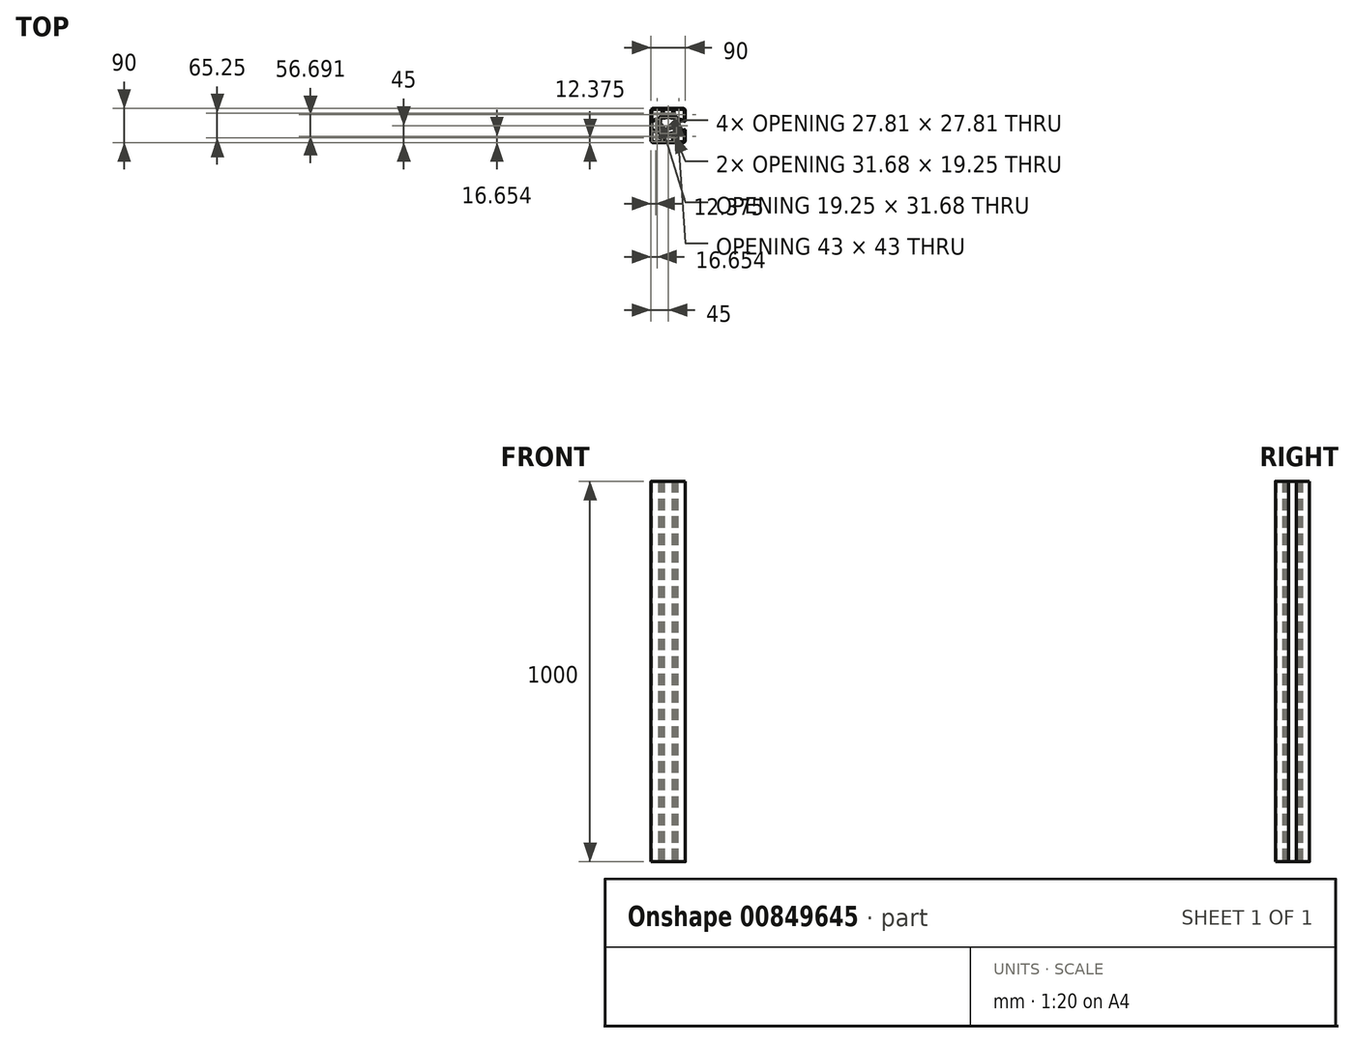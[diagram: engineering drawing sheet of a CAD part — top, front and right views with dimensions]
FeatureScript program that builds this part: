
annotation { "Feature Type Name" : "Feature", "Feature Type Description" : "" }
export const myFeature = defineFeature(function(context is Context, id is Id, definition is map)
    precondition{}
    {
        {
            var Q0;
            Q0=qCreatedBy(makeId("Top.planeOp"),FACE);
            var sketch = newSketch(context, id + "F0", { "sketchPlane" : qUnion([Q0])});
            skLineSegment(sketch, "E0", {"start": v(-42.25, -10.99) * mm, "end": v(-42.25, 10.99) * mm});
            skLineSegment(sketch, "E1", {"start": v(-24.26, -15.8) * mm, "end": v(-42.25, -10.99) * mm});
            skLineSegment(sketch, "E2", {"start": v(-23, -9.27) * mm, "end": v(-23, -14.84) * mm});
            skLineSegment(sketch, "E3", {"start": v(-23, 14.84) * mm, "end": v(-23, 9.27) * mm});
            skLineSegment(sketch, "E4", {"start": v(-42.25, 10.99) * mm, "end": v(-24.26, 15.8) * mm});
            skLineSegment(sketch, "E5", {"start": v(-39.73, -14.5) * mm, "end": v(-24.48, -18.6) * mm});
            skLineSegment(sketch, "E6", {"start": v(-42.25, -39) * mm, "end": v(-42.25, -16.44) * mm});
            skLineSegment(sketch, "E7", {"start": v(-16.44, -42.25) * mm, "end": v(-39, -42.25) * mm});
            skLineSegment(sketch, "E8", {"start": v(-18.6, -24.48) * mm, "end": v(-14.5, -39.73) * mm});
            skLineSegment(sketch, "E9", {"start": v(-21, -23) * mm, "end": v(-20.53, -23) * mm});
            skLineSegment(sketch, "E10", {"start": v(-23, -20.53) * mm, "end": v(-23, -21) * mm});
            skLineSegment(sketch, "E11", {"start": v(14.5, -39.73) * mm, "end": v(18.6, -24.48) * mm});
            skLineSegment(sketch, "E12", {"start": v(39, -42.25) * mm, "end": v(16.44, -42.25) * mm});
            skLineSegment(sketch, "E13", {"start": v(42.25, -16.44) * mm, "end": v(42.25, -39) * mm});
            skLineSegment(sketch, "E14", {"start": v(24.48, -18.6) * mm, "end": v(39.73, -14.5) * mm});
            skLineSegment(sketch, "E15", {"start": v(23, -21) * mm, "end": v(23, -20.53) * mm});
            skLineSegment(sketch, "E16", {"start": v(20.53, -23) * mm, "end": v(21, -23) * mm});
            skLineSegment(sketch, "E17", {"start": v(14.84, 23) * mm, "end": v(9.27, 23) * mm});
            skLineSegment(sketch, "E18", {"start": v(10.99, 42.25) * mm, "end": v(15.8, 24.26) * mm});
            skLineSegment(sketch, "E19", {"start": v(-10.99, 42.25) * mm, "end": v(10.99, 42.25) * mm});
            skLineSegment(sketch, "E20", {"start": v(-15.8, 24.26) * mm, "end": v(-10.99, 42.25) * mm});
            skLineSegment(sketch, "E21", {"start": v(-9.27, 23) * mm, "end": v(-14.84, 23) * mm});
            skLineSegment(sketch, "E22", {"start": v(23, 14.84) * mm, "end": v(23, 9.27) * mm});
            skLineSegment(sketch, "E23", {"start": v(23, -9.27) * mm, "end": v(23, -14.84) * mm});
            skLineSegment(sketch, "E24", {"start": v(24.26, -15.8) * mm, "end": v(43.43, -10.67) * mm});
            skLineSegment(sketch, "E25", {"start": v(45, -11.88) * mm, "end": v(45, -39) * mm});
            skLineSegment(sketch, "E26", {"start": v(39, -45) * mm, "end": v(-39, -45) * mm});
            skLineSegment(sketch, "E27", {"start": v(-45, -39) * mm, "end": v(-45, 39) * mm});
            skLineSegment(sketch, "E28", {"start": v(-39, 45) * mm, "end": v(39, 45) * mm});
            skLineSegment(sketch, "E29", {"start": v(45, 39) * mm, "end": v(45, 11.88) * mm});
            skLineSegment(sketch, "E30", {"start": v(43.43, 10.67) * mm, "end": v(24.26, 15.8) * mm});
            skLineSegment(sketch, "E31", {"start": v(20.25, 19.25) * mm, "end": v(20.25, 7.4) * mm});
            skLineSegment(sketch, "E32", {"start": v(7.4, 20.25) * mm, "end": v(19.25, 20.25) * mm});
            skLineSegment(sketch, "E33", {"start": v(-19.25, 20.25) * mm, "end": v(-7.4, 20.25) * mm});
            skLineSegment(sketch, "E34", {"start": v(-20.25, 7.4) * mm, "end": v(-20.25, 19.25) * mm});
            skLineSegment(sketch, "E35", {"start": v(-20.25, -19.25) * mm, "end": v(-20.25, -7.4) * mm});
            skLineSegment(sketch, "E36", {"start": v(-7.4, -20.25) * mm, "end": v(-19.25, -20.25) * mm});
            skLineSegment(sketch, "E37", {"start": v(19.25, -20.25) * mm, "end": v(7.4, -20.25) * mm});
            skLineSegment(sketch, "E38", {"start": v(20.25, -7.4) * mm, "end": v(20.25, -19.25) * mm});
            skLineSegment(sketch, "E39", {"start": v(39.73, 14.5) * mm, "end": v(24.48, 18.6) * mm});
            skLineSegment(sketch, "E40", {"start": v(42.25, 39) * mm, "end": v(42.25, 16.44) * mm});
            skLineSegment(sketch, "E41", {"start": v(16.44, 42.25) * mm, "end": v(39, 42.25) * mm});
            skLineSegment(sketch, "E42", {"start": v(18.6, 24.48) * mm, "end": v(14.5, 39.73) * mm});
            skLineSegment(sketch, "E43", {"start": v(21, 23) * mm, "end": v(20.53, 23) * mm});
            skLineSegment(sketch, "E44", {"start": v(23, 20.53) * mm, "end": v(23, 21) * mm});
            skLineSegment(sketch, "E45", {"start": v(-14.5, 39.73) * mm, "end": v(-18.6, 24.48) * mm});
            skLineSegment(sketch, "E46", {"start": v(-39, 42.25) * mm, "end": v(-16.44, 42.25) * mm});
            skLineSegment(sketch, "E47", {"start": v(-42.25, 16.44) * mm, "end": v(-42.25, 39) * mm});
            skLineSegment(sketch, "E48", {"start": v(-24.48, 18.6) * mm, "end": v(-39.73, 14.5) * mm});
            skLineSegment(sketch, "E49", {"start": v(-23, 21) * mm, "end": v(-23, 20.53) * mm});
            skLineSegment(sketch, "E50", {"start": v(-20.53, 23) * mm, "end": v(-21, 23) * mm});
            skLineSegment(sketch, "E51", {"start": v(10.99, -42.25) * mm, "end": v(-10.99, -42.25) * mm});
            skLineSegment(sketch, "E52", {"start": v(15.8, -24.26) * mm, "end": v(10.99, -42.25) * mm});
            skLineSegment(sketch, "E53", {"start": v(9.27, -23) * mm, "end": v(14.84, -23) * mm});
            skLineSegment(sketch, "E54", {"start": v(-14.84, -23) * mm, "end": v(-9.27, -23) * mm});
            skLineSegment(sketch, "E55", {"start": v(-10.99, -42.25) * mm, "end": v(-15.8, -24.26) * mm});
            skArc(sketch, "E56", {"start": v(-24.26, -15.8) * mm, "mid": v(-23.4, -15.64) * mm, "end": v(-23, -14.84) * mm});
            skArc(sketch, "E57", {"start": v(-23, -9.27) * mm, "mid": v(-23.02, -9.06) * mm, "end": v(-23.09, -8.86) * mm});
            skArc(sketch, "E58", {"start": v(-23.09, 8.86) * mm, "mid": v(-25, 0) * mm, "end": v(-23.09, -8.86) * mm});
            skArc(sketch, "E59", {"start": v(-23.09, 8.86) * mm, "mid": v(-23.02, 9.06) * mm, "end": v(-23, 9.27) * mm});
            skArc(sketch, "E60", {"start": v(-23, 14.84) * mm, "mid": v(-23.4, 15.64) * mm, "end": v(-24.26, 15.8) * mm});
            skArc(sketch, "E61", {"start": v(-23, -20.53) * mm, "mid": v(-23.41, -19.3) * mm, "end": v(-24.48, -18.6) * mm});
            skArc(sketch, "E62", {"start": v(-39.73, -14.5) * mm, "mid": v(-41.47, -14.85) * mm, "end": v(-42.25, -16.44) * mm});
            skArc(sketch, "E63", {"start": v(-42.25, -39) * mm, "mid": v(-41.3, -41.3) * mm, "end": v(-39, -42.25) * mm});
            skArc(sketch, "E64", {"start": v(-16.44, -42.25) * mm, "mid": v(-14.85, -41.47) * mm, "end": v(-14.5, -39.73) * mm});
            skArc(sketch, "E65", {"start": v(-18.6, -24.48) * mm, "mid": v(-19.3, -23.41) * mm, "end": v(-20.53, -23) * mm});
            skArc(sketch, "E66", {"start": v(-23, -21) * mm, "mid": v(-22.41, -22.41) * mm, "end": v(-21, -23) * mm});
            skArc(sketch, "E67", {"start": v(20.53, -23) * mm, "mid": v(19.3, -23.41) * mm, "end": v(18.6, -24.48) * mm});
            skArc(sketch, "E68", {"start": v(14.5, -39.73) * mm, "mid": v(14.85, -41.47) * mm, "end": v(16.44, -42.25) * mm});
            skArc(sketch, "E69", {"start": v(39, -42.25) * mm, "mid": v(41.3, -41.3) * mm, "end": v(42.25, -39) * mm});
            skArc(sketch, "E70", {"start": v(42.25, -16.44) * mm, "mid": v(41.47, -14.85) * mm, "end": v(39.73, -14.5) * mm});
            skArc(sketch, "E71", {"start": v(24.48, -18.6) * mm, "mid": v(23.41, -19.3) * mm, "end": v(23, -20.53) * mm});
            skArc(sketch, "E72", {"start": v(21, -23) * mm, "mid": v(22.41, -22.41) * mm, "end": v(23, -21) * mm});
            skArc(sketch, "E73", {"start": v(-9.27, 23) * mm, "mid": v(-9.06, 23.02) * mm, "end": v(-8.86, 23.09) * mm});
            skArc(sketch, "E74", {"start": v(8.86, 23.09) * mm, "mid": v(0, 25) * mm, "end": v(-8.86, 23.09) * mm});
            skArc(sketch, "E75", {"start": v(8.86, 23.09) * mm, "mid": v(9.06, 23.02) * mm, "end": v(9.27, 23) * mm});
            skArc(sketch, "E76", {"start": v(14.84, 23) * mm, "mid": v(15.64, 23.4) * mm, "end": v(15.8, 24.26) * mm});
            skArc(sketch, "E77", {"start": v(-15.8, 24.26) * mm, "mid": v(-15.64, 23.4) * mm, "end": v(-14.84, 23) * mm});
            skArc(sketch, "E78", {"start": v(24.26, 15.8) * mm, "mid": v(23.4, 15.64) * mm, "end": v(23, 14.84) * mm});
            skArc(sketch, "E79", {"start": v(23, 9.27) * mm, "mid": v(23.02, 9.06) * mm, "end": v(23.09, 8.86) * mm});
            skArc(sketch, "E80", {"start": v(23.09, -8.86) * mm, "mid": v(25, 0) * mm, "end": v(23.09, 8.86) * mm});
            skArc(sketch, "E81", {"start": v(23.09, -8.86) * mm, "mid": v(23.02, -9.06) * mm, "end": v(23, -9.27) * mm});
            skArc(sketch, "E82", {"start": v(23, -14.84) * mm, "mid": v(23.4, -15.64) * mm, "end": v(24.26, -15.8) * mm});
            skArc(sketch, "E83", {"start": v(45, -11.88) * mm, "mid": v(44.51, -10.89) * mm, "end": v(43.43, -10.67) * mm});
            skArc(sketch, "E84", {"start": v(39, -45) * mm, "mid": v(43.24, -43.24) * mm, "end": v(45, -39) * mm});
            skArc(sketch, "E85", {"start": v(-45, -39) * mm, "mid": v(-43.24, -43.24) * mm, "end": v(-39, -45) * mm});
            skArc(sketch, "E86", {"start": v(-39, 45) * mm, "mid": v(-43.24, 43.24) * mm, "end": v(-45, 39) * mm});
            skArc(sketch, "E87", {"start": v(45, 39) * mm, "mid": v(43.24, 43.24) * mm, "end": v(39, 45) * mm});
            skArc(sketch, "E88", {"start": v(43.43, 10.67) * mm, "mid": v(44.51, 10.89) * mm, "end": v(45, 11.88) * mm});
            skArc(sketch, "E89", {"start": v(20.25, 7.4) * mm, "mid": v(20.26, 7.23) * mm, "end": v(20.3, 7.07) * mm});
            skArc(sketch, "E90", {"start": v(20.25, 19.25) * mm, "mid": v(19.96, 19.96) * mm, "end": v(19.25, 20.25) * mm});
            skArc(sketch, "E91", {"start": v(7.07, 20.3) * mm, "mid": v(7.23, 20.26) * mm, "end": v(7.4, 20.25) * mm});
            skArc(sketch, "E92", {"start": v(7.07, 20.3) * mm, "mid": v(0, 21.5) * mm, "end": v(-7.07, 20.3) * mm});
            skArc(sketch, "E93", {"start": v(-7.4, 20.25) * mm, "mid": v(-7.23, 20.26) * mm, "end": v(-7.07, 20.3) * mm});
            skArc(sketch, "E94", {"start": v(-19.25, 20.25) * mm, "mid": v(-19.96, 19.96) * mm, "end": v(-20.25, 19.25) * mm});
            skArc(sketch, "E95", {"start": v(-20.3, 7.07) * mm, "mid": v(-20.26, 7.23) * mm, "end": v(-20.25, 7.4) * mm});
            skArc(sketch, "E96", {"start": v(-20.3, 7.07) * mm, "mid": v(-21.5, 0) * mm, "end": v(-20.3, -7.07) * mm});
            skArc(sketch, "E97", {"start": v(-20.25, -7.4) * mm, "mid": v(-20.26, -7.23) * mm, "end": v(-20.3, -7.07) * mm});
            skArc(sketch, "E98", {"start": v(-20.25, -19.25) * mm, "mid": v(-19.96, -19.96) * mm, "end": v(-19.25, -20.25) * mm});
            skArc(sketch, "E99", {"start": v(-7.07, -20.3) * mm, "mid": v(-7.23, -20.26) * mm, "end": v(-7.4, -20.25) * mm});
            skArc(sketch, "E100", {"start": v(-7.07, -20.3) * mm, "mid": v(0, -21.5) * mm, "end": v(7.07, -20.3) * mm});
            skArc(sketch, "E101", {"start": v(7.4, -20.25) * mm, "mid": v(7.23, -20.26) * mm, "end": v(7.07, -20.3) * mm});
            skArc(sketch, "E102", {"start": v(19.25, -20.25) * mm, "mid": v(19.96, -19.96) * mm, "end": v(20.25, -19.25) * mm});
            skArc(sketch, "E103", {"start": v(20.3, -7.07) * mm, "mid": v(20.26, -7.23) * mm, "end": v(20.25, -7.4) * mm});
            skArc(sketch, "E104", {"start": v(20.3, -7.07) * mm, "mid": v(21.5, 0) * mm, "end": v(20.3, 7.07) * mm});
            skArc(sketch, "E105", {"start": v(23, 20.53) * mm, "mid": v(23.41, 19.3) * mm, "end": v(24.48, 18.6) * mm});
            skArc(sketch, "E106", {"start": v(39.73, 14.5) * mm, "mid": v(41.47, 14.85) * mm, "end": v(42.25, 16.44) * mm});
            skArc(sketch, "E107", {"start": v(42.25, 39) * mm, "mid": v(41.3, 41.3) * mm, "end": v(39, 42.25) * mm});
            skArc(sketch, "E108", {"start": v(16.44, 42.25) * mm, "mid": v(14.85, 41.47) * mm, "end": v(14.5, 39.73) * mm});
            skArc(sketch, "E109", {"start": v(18.6, 24.48) * mm, "mid": v(19.3, 23.41) * mm, "end": v(20.53, 23) * mm});
            skArc(sketch, "E110", {"start": v(23, 21) * mm, "mid": v(22.41, 22.41) * mm, "end": v(21, 23) * mm});
            skArc(sketch, "E111", {"start": v(-20.53, 23) * mm, "mid": v(-19.3, 23.41) * mm, "end": v(-18.6, 24.48) * mm});
            skArc(sketch, "E112", {"start": v(-14.5, 39.73) * mm, "mid": v(-14.85, 41.47) * mm, "end": v(-16.44, 42.25) * mm});
            skArc(sketch, "E113", {"start": v(-39, 42.25) * mm, "mid": v(-41.3, 41.3) * mm, "end": v(-42.25, 39) * mm});
            skArc(sketch, "E114", {"start": v(-42.25, 16.44) * mm, "mid": v(-41.47, 14.85) * mm, "end": v(-39.73, 14.5) * mm});
            skArc(sketch, "E115", {"start": v(-24.48, 18.6) * mm, "mid": v(-23.41, 19.3) * mm, "end": v(-23, 20.53) * mm});
            skArc(sketch, "E116", {"start": v(-21, 23) * mm, "mid": v(-22.41, 22.41) * mm, "end": v(-23, 21) * mm});
            skArc(sketch, "E117", {"start": v(15.8, -24.26) * mm, "mid": v(15.64, -23.4) * mm, "end": v(14.84, -23) * mm});
            skArc(sketch, "E118", {"start": v(9.27, -23) * mm, "mid": v(9.06, -23.02) * mm, "end": v(8.86, -23.09) * mm});
            skArc(sketch, "E119", {"start": v(-8.86, -23.09) * mm, "mid": v(-9.06, -23.02) * mm, "end": v(-9.27, -23) * mm});
            skArc(sketch, "E120", {"start": v(-14.84, -23) * mm, "mid": v(-15.64, -23.4) * mm, "end": v(-15.8, -24.26) * mm});
            skArc(sketch, "E121", {"start": v(-8.86, -23.09) * mm, "mid": v(0, -25) * mm, "end": v(8.86, -23.09) * mm});
            skArc(sketch, "E122.1.0.0", {"start": v(55, -39) * mm, "mid": v(56.76, -43.24) * mm, "end": v(61, -45) * mm});
            skLineSegment(sketch, "E122.1.0.1", {"start": v(55, -39) * mm, "end": v(55, 39) * mm});
            skArc(sketch, "E122.1.0.2", {"start": v(57.75, -39) * mm, "mid": v(58.7, -41.3) * mm, "end": v(61, -42.25) * mm});
            skLineSegment(sketch, "E122.1.0.3", {"start": v(139, -45) * mm, "end": v(61, -45) * mm});
            skLineSegment(sketch, "E122.1.0.4", {"start": v(57.75, -39) * mm, "end": v(57.75, -16.44) * mm});
            skLineSegment(sketch, "E122.1.0.5", {"start": v(83.56, -42.25) * mm, "end": v(61, -42.25) * mm});
            skLineSegment(sketch, "E122.1.0.6", {"start": v(61, 45) * mm, "end": v(139, 45) * mm});
            skArc(sketch, "E122.1.0.7", {"start": v(145, 39) * mm, "mid": v(143.24, 43.24) * mm, "end": v(139, 45) * mm});
            skLineSegment(sketch, "E122.1.0.8", {"start": v(145, 39) * mm, "end": v(145, 11.88) * mm});
            skLineSegment(sketch, "E122.1.0.9", {"start": v(142.25, 39) * mm, "end": v(142.25, 16.44) * mm});
            skLineSegment(sketch, "E122.1.0.10", {"start": v(116.44, 42.25) * mm, "end": v(139, 42.25) * mm});
            skArc(sketch, "E122.1.0.11", {"start": v(142.25, 39) * mm, "mid": v(141.3, 41.3) * mm, "end": v(139, 42.25) * mm});
            skLineSegment(sketch, "E122.1.0.12", {"start": v(57.75, -10.99) * mm, "end": v(57.75, 10.99) * mm});
            skLineSegment(sketch, "E122.1.0.13", {"start": v(89.01, 42.25) * mm, "end": v(110.99, 42.25) * mm});
            skLineSegment(sketch, "E122.1.0.14", {"start": v(142.25, -16.44) * mm, "end": v(142.25, -39) * mm});
            skLineSegment(sketch, "E122.1.0.15", {"start": v(139, -42.25) * mm, "end": v(116.44, -42.25) * mm});
            skLineSegment(sketch, "E122.1.0.16", {"start": v(145, -11.88) * mm, "end": v(145, -39) * mm});
            skArc(sketch, "E122.1.0.17", {"start": v(139, -42.25) * mm, "mid": v(141.3, -41.3) * mm, "end": v(142.25, -39) * mm});
            skArc(sketch, "E122.1.0.18", {"start": v(139, -45) * mm, "mid": v(143.24, -43.24) * mm, "end": v(145, -39) * mm});
            skArc(sketch, "E122.1.0.19", {"start": v(79.47, 23) * mm, "mid": v(80.7, 23.41) * mm, "end": v(81.4, 24.48) * mm});
            skLineSegment(sketch, "E122.1.0.20", {"start": v(60.27, -14.5) * mm, "end": v(75.52, -18.6) * mm});
            skArc(sketch, "E122.1.0.21", {"start": v(61, 42.25) * mm, "mid": v(58.7, 41.3) * mm, "end": v(57.75, 39) * mm});
            skLineSegment(sketch, "E122.1.0.22", {"start": v(57.75, 10.99) * mm, "end": v(75.74, 15.8) * mm});
            skLineSegment(sketch, "E122.1.0.23", {"start": v(57.75, 16.44) * mm, "end": v(57.75, 39) * mm});
            skArc(sketch, "E122.1.0.24", {"start": v(60.27, -14.5) * mm, "mid": v(58.53, -14.85) * mm, "end": v(57.75, -16.44) * mm});
            skLineSegment(sketch, "E122.1.0.25", {"start": v(61, 42.25) * mm, "end": v(83.56, 42.25) * mm});
            skArc(sketch, "E122.1.0.26", {"start": v(80.75, 20.25) * mm, "mid": v(80.04, 19.96) * mm, "end": v(79.75, 19.25) * mm});
            skArc(sketch, "E122.1.0.27", {"start": v(61, 45) * mm, "mid": v(56.76, 43.24) * mm, "end": v(55, 39) * mm});
            skLineSegment(sketch, "E122.1.0.28", {"start": v(75.52, 18.6) * mm, "end": v(60.27, 14.5) * mm});
            skLineSegment(sketch, "E122.1.0.29", {"start": v(75.74, -15.8) * mm, "end": v(57.75, -10.99) * mm});
            skArc(sketch, "E122.1.0.30", {"start": v(57.75, 16.44) * mm, "mid": v(58.53, 14.85) * mm, "end": v(60.27, 14.5) * mm});
            skLineSegment(sketch, "E122.1.0.31", {"start": v(85.5, 39.73) * mm, "end": v(81.4, 24.48) * mm});
            skArc(sketch, "E122.1.0.32", {"start": v(81.4, -24.48) * mm, "mid": v(80.7, -23.41) * mm, "end": v(79.47, -23) * mm});
            skLineSegment(sketch, "E122.1.0.33", {"start": v(77, -9.27) * mm, "end": v(77, -14.84) * mm});
            skArc(sketch, "E122.1.0.34", {"start": v(79.7, 7.07) * mm, "mid": v(79.74, 7.23) * mm, "end": v(79.75, 7.4) * mm});
            skLineSegment(sketch, "E122.1.0.35", {"start": v(77, 21) * mm, "end": v(77, 20.53) * mm});
            skArc(sketch, "E122.1.0.36", {"start": v(109.27, -23) * mm, "mid": v(109.06, -23.02) * mm, "end": v(108.86, -23.09) * mm});
            skArc(sketch, "E122.1.0.37", {"start": v(92.93, -20.3) * mm, "mid": v(100, -21.5) * mm, "end": v(107.07, -20.3) * mm});
            skLineSegment(sketch, "E122.1.0.38", {"start": v(80.75, 20.25) * mm, "end": v(92.6, 20.25) * mm});
            skLineSegment(sketch, "E122.1.0.39", {"start": v(114.5, -39.73) * mm, "end": v(118.6, -24.48) * mm});
            skLineSegment(sketch, "E122.1.0.40", {"start": v(110.99, -42.25) * mm, "end": v(89.01, -42.25) * mm});
            skArc(sketch, "E122.1.0.41", {"start": v(79.75, -7.4) * mm, "mid": v(79.74, -7.23) * mm, "end": v(79.7, -7.07) * mm});
            skLineSegment(sketch, "E122.1.0.42", {"start": v(81.4, -24.48) * mm, "end": v(85.5, -39.73) * mm});
            skLineSegment(sketch, "E122.1.0.43", {"start": v(79.75, -19.25) * mm, "end": v(79.75, -7.4) * mm});
            skArc(sketch, "E122.1.0.44", {"start": v(92.93, -20.3) * mm, "mid": v(92.77, -20.26) * mm, "end": v(92.6, -20.25) * mm});
            skArc(sketch, "E122.1.0.45", {"start": v(76.91, 8.86) * mm, "mid": v(75, 0) * mm, "end": v(76.91, -8.86) * mm});
            skLineSegment(sketch, "E122.1.0.46", {"start": v(85.16, -23) * mm, "end": v(90.73, -23) * mm});
            skArc(sketch, "E122.1.0.47", {"start": v(120.53, -23) * mm, "mid": v(119.3, -23.41) * mm, "end": v(118.6, -24.48) * mm});
            skArc(sketch, "E122.1.0.48", {"start": v(85.16, -23) * mm, "mid": v(84.36, -23.4) * mm, "end": v(84.2, -24.26) * mm});
            skLineSegment(sketch, "E122.1.0.49", {"start": v(115.8, -24.26) * mm, "end": v(110.99, -42.25) * mm});
            skArc(sketch, "E122.1.0.50", {"start": v(75.52, 18.6) * mm, "mid": v(76.59, 19.3) * mm, "end": v(77, 20.53) * mm});
            skArc(sketch, "E122.1.0.51", {"start": v(83.56, -42.25) * mm, "mid": v(85.15, -41.47) * mm, "end": v(85.5, -39.73) * mm});
            skArc(sketch, "E122.1.0.52", {"start": v(77, -9.27) * mm, "mid": v(76.98, -9.06) * mm, "end": v(76.91, -8.86) * mm});
            skArc(sketch, "E122.1.0.53", {"start": v(107.4, -20.25) * mm, "mid": v(107.23, -20.26) * mm, "end": v(107.07, -20.3) * mm});
            skArc(sketch, "E122.1.0.54", {"start": v(79.7, 7.07) * mm, "mid": v(78.5, 0) * mm, "end": v(79.7, -7.07) * mm});
            skLineSegment(sketch, "E122.1.0.55", {"start": v(90.73, 23) * mm, "end": v(85.16, 23) * mm});
            skArc(sketch, "E122.1.0.56", {"start": v(91.14, -23.09) * mm, "mid": v(100, -25) * mm, "end": v(108.86, -23.09) * mm});
            skLineSegment(sketch, "E122.1.0.57", {"start": v(92.6, -20.25) * mm, "end": v(80.75, -20.25) * mm});
            skLineSegment(sketch, "E122.1.0.58", {"start": v(79.75, 7.4) * mm, "end": v(79.75, 19.25) * mm});
            skLineSegment(sketch, "E122.1.0.59", {"start": v(119.25, -20.25) * mm, "end": v(107.4, -20.25) * mm});
            skLineSegment(sketch, "E122.1.0.60", {"start": v(89.01, -42.25) * mm, "end": v(84.2, -24.26) * mm});
            skLineSegment(sketch, "E122.1.0.61", {"start": v(77, -20.53) * mm, "end": v(77, -21) * mm});
            skArc(sketch, "E122.1.0.62", {"start": v(114.5, -39.73) * mm, "mid": v(114.85, -41.47) * mm, "end": v(116.44, -42.25) * mm});
            skArc(sketch, "E122.1.0.63", {"start": v(91.14, -23.09) * mm, "mid": v(90.94, -23.02) * mm, "end": v(90.73, -23) * mm});
            skArc(sketch, "E122.1.0.64", {"start": v(108.86, 23.09) * mm, "mid": v(100, 25) * mm, "end": v(91.14, 23.09) * mm});
            skLineSegment(sketch, "E122.1.0.65", {"start": v(109.27, -23) * mm, "end": v(114.84, -23) * mm});
            skLineSegment(sketch, "E122.1.0.66", {"start": v(77, 14.84) * mm, "end": v(77, 9.27) * mm});
            skLineSegment(sketch, "E122.1.0.67", {"start": v(79.47, 23) * mm, "end": v(79, 23) * mm});
            skArc(sketch, "E122.1.0.68", {"start": v(115.8, -24.26) * mm, "mid": v(115.64, -23.4) * mm, "end": v(114.84, -23) * mm});
            skLineSegment(sketch, "E122.1.0.69", {"start": v(84.2, 24.26) * mm, "end": v(89.01, 42.25) * mm});
            skArc(sketch, "E122.1.0.70", {"start": v(75.74, -15.8) * mm, "mid": v(76.6, -15.64) * mm, "end": v(77, -14.84) * mm});
            skLineSegment(sketch, "E122.1.0.71", {"start": v(79, -23) * mm, "end": v(79.47, -23) * mm});
            skArc(sketch, "E122.1.0.72", {"start": v(77, 14.84) * mm, "mid": v(76.6, 15.64) * mm, "end": v(75.74, 15.8) * mm});
            skArc(sketch, "E122.1.0.73", {"start": v(84.2, 24.26) * mm, "mid": v(84.36, 23.4) * mm, "end": v(85.16, 23) * mm});
            skArc(sketch, "E122.1.0.74", {"start": v(107.07, 20.3) * mm, "mid": v(100, 21.5) * mm, "end": v(92.93, 20.3) * mm});
            skArc(sketch, "E122.1.0.75", {"start": v(77, -21) * mm, "mid": v(77.59, -22.41) * mm, "end": v(79, -23) * mm});
            skArc(sketch, "E122.1.0.76", {"start": v(92.6, 20.25) * mm, "mid": v(92.77, 20.26) * mm, "end": v(92.93, 20.3) * mm});
            skArc(sketch, "E122.1.0.77", {"start": v(79, 23) * mm, "mid": v(77.59, 22.41) * mm, "end": v(77, 21) * mm});
            skArc(sketch, "E122.1.0.78", {"start": v(79.75, -19.25) * mm, "mid": v(80.04, -19.96) * mm, "end": v(80.75, -20.25) * mm});
            skArc(sketch, "E122.1.0.79", {"start": v(90.73, 23) * mm, "mid": v(90.94, 23.02) * mm, "end": v(91.14, 23.09) * mm});
            skArc(sketch, "E122.1.0.80", {"start": v(76.91, 8.86) * mm, "mid": v(76.98, 9.06) * mm, "end": v(77, 9.27) * mm});
            skArc(sketch, "E122.1.0.81", {"start": v(77, -20.53) * mm, "mid": v(76.59, -19.3) * mm, "end": v(75.52, -18.6) * mm});
            skLineSegment(sketch, "E122.1.0.82", {"start": v(139.73, 14.5) * mm, "end": v(124.48, 18.6) * mm});
            skLineSegment(sketch, "E122.1.0.83", {"start": v(118.6, 24.48) * mm, "end": v(114.5, 39.73) * mm});
            skArc(sketch, "E122.1.0.84", {"start": v(124.26, 15.8) * mm, "mid": v(123.4, 15.64) * mm, "end": v(123, 14.84) * mm});
            skArc(sketch, "E122.1.0.85", {"start": v(119.25, -20.25) * mm, "mid": v(119.96, -19.96) * mm, "end": v(120.25, -19.25) * mm});
            skLineSegment(sketch, "E122.1.0.86", {"start": v(143.43, 10.67) * mm, "end": v(124.26, 15.8) * mm});
            skArc(sketch, "E122.1.0.87", {"start": v(85.5, 39.73) * mm, "mid": v(85.15, 41.47) * mm, "end": v(83.56, 42.25) * mm});
            skArc(sketch, "E122.1.0.88", {"start": v(123, 21) * mm, "mid": v(122.41, 22.41) * mm, "end": v(121, 23) * mm});
            skArc(sketch, "E122.1.0.89", {"start": v(139.73, 14.5) * mm, "mid": v(141.47, 14.85) * mm, "end": v(142.25, 16.44) * mm});
            skArc(sketch, "E122.1.0.90", {"start": v(123.09, -8.86) * mm, "mid": v(125, 0) * mm, "end": v(123.09, 8.86) * mm});
            skArc(sketch, "E122.1.0.91", {"start": v(120.3, -7.07) * mm, "mid": v(121.5, 0) * mm, "end": v(120.3, 7.07) * mm});
            skLineSegment(sketch, "E122.1.0.92", {"start": v(114.84, 23) * mm, "end": v(109.27, 23) * mm});
            skArc(sketch, "E122.1.0.93", {"start": v(123, 9.27) * mm, "mid": v(123.02, 9.06) * mm, "end": v(123.09, 8.86) * mm});
            skLineSegment(sketch, "E122.1.0.94", {"start": v(124.26, -15.8) * mm, "end": v(143.43, -10.67) * mm});
            skArc(sketch, "E122.1.0.95", {"start": v(142.25, -16.44) * mm, "mid": v(141.47, -14.85) * mm, "end": v(139.73, -14.5) * mm});
            skArc(sketch, "E122.1.0.96", {"start": v(123.09, -8.86) * mm, "mid": v(123.02, -9.06) * mm, "end": v(123, -9.27) * mm});
            skArc(sketch, "E122.1.0.97", {"start": v(123, -14.84) * mm, "mid": v(123.4, -15.64) * mm, "end": v(124.26, -15.8) * mm});
            skArc(sketch, "E122.1.0.98", {"start": v(116.44, 42.25) * mm, "mid": v(114.85, 41.47) * mm, "end": v(114.5, 39.73) * mm});
            skArc(sketch, "E122.1.0.99", {"start": v(145, -11.88) * mm, "mid": v(144.51, -10.89) * mm, "end": v(143.43, -10.67) * mm});
            skLineSegment(sketch, "E122.1.0.100", {"start": v(123, 20.53) * mm, "end": v(123, 21) * mm});
            skLineSegment(sketch, "E122.1.0.101", {"start": v(123, -9.27) * mm, "end": v(123, -14.84) * mm});
            skLineSegment(sketch, "E122.1.0.102", {"start": v(120.25, 19.25) * mm, "end": v(120.25, 7.4) * mm});
            skLineSegment(sketch, "E122.1.0.103", {"start": v(120.25, -7.4) * mm, "end": v(120.25, -19.25) * mm});
            skLineSegment(sketch, "E122.1.0.104", {"start": v(110.99, 42.25) * mm, "end": v(115.8, 24.26) * mm});
            skLineSegment(sketch, "E122.1.0.105", {"start": v(107.4, 20.25) * mm, "end": v(119.25, 20.25) * mm});
            skArc(sketch, "E122.1.0.106", {"start": v(143.43, 10.67) * mm, "mid": v(144.51, 10.89) * mm, "end": v(145, 11.88) * mm});
            skArc(sketch, "E122.1.0.107", {"start": v(114.84, 23) * mm, "mid": v(115.64, 23.4) * mm, "end": v(115.8, 24.26) * mm});
            skLineSegment(sketch, "E122.1.0.108", {"start": v(124.48, -18.6) * mm, "end": v(139.73, -14.5) * mm});
            skLineSegment(sketch, "E122.1.0.109", {"start": v(123, 14.84) * mm, "end": v(123, 9.27) * mm});
            skArc(sketch, "E122.1.0.110", {"start": v(118.6, 24.48) * mm, "mid": v(119.3, 23.41) * mm, "end": v(120.53, 23) * mm});
            skArc(sketch, "E122.1.0.111", {"start": v(120.25, 19.25) * mm, "mid": v(119.96, 19.96) * mm, "end": v(119.25, 20.25) * mm});
            skArc(sketch, "E122.1.0.112", {"start": v(108.86, 23.09) * mm, "mid": v(109.06, 23.02) * mm, "end": v(109.27, 23) * mm});
            skArc(sketch, "E122.1.0.113", {"start": v(120.3, -7.07) * mm, "mid": v(120.26, -7.23) * mm, "end": v(120.25, -7.4) * mm});
            skArc(sketch, "E122.1.0.114", {"start": v(121, -23) * mm, "mid": v(122.41, -22.41) * mm, "end": v(123, -21) * mm});
            skArc(sketch, "E122.1.0.115", {"start": v(107.07, 20.3) * mm, "mid": v(107.23, 20.26) * mm, "end": v(107.4, 20.25) * mm});
            skArc(sketch, "E122.1.0.116", {"start": v(120.25, 7.4) * mm, "mid": v(120.26, 7.23) * mm, "end": v(120.3, 7.07) * mm});
            skArc(sketch, "E122.1.0.117", {"start": v(123, 20.53) * mm, "mid": v(123.41, 19.3) * mm, "end": v(124.48, 18.6) * mm});
            skLineSegment(sketch, "E122.1.0.118", {"start": v(123, -21) * mm, "end": v(123, -20.53) * mm});
            skLineSegment(sketch, "E122.1.0.119", {"start": v(121, 23) * mm, "end": v(120.53, 23) * mm});
            skLineSegment(sketch, "E122.1.0.120", {"start": v(120.53, -23) * mm, "end": v(121, -23) * mm});
            skArc(sketch, "E122.1.0.121", {"start": v(124.48, -18.6) * mm, "mid": v(123.41, -19.3) * mm, "end": v(123, -20.53) * mm});
            skArc(sketch, "E122.2.0.0", {"start": v(155, -39) * mm, "mid": v(156.76, -43.24) * mm, "end": v(161, -45) * mm});
            skLineSegment(sketch, "E122.2.0.1", {"start": v(155, -39) * mm, "end": v(155, 39) * mm});
            skArc(sketch, "E122.2.0.2", {"start": v(157.75, -39) * mm, "mid": v(158.7, -41.3) * mm, "end": v(161, -42.25) * mm});
            skLineSegment(sketch, "E122.2.0.3", {"start": v(239, -45) * mm, "end": v(161, -45) * mm});
            skLineSegment(sketch, "E122.2.0.4", {"start": v(157.75, -39) * mm, "end": v(157.75, -16.44) * mm});
            skLineSegment(sketch, "E122.2.0.5", {"start": v(183.56, -42.25) * mm, "end": v(161, -42.25) * mm});
            skLineSegment(sketch, "E122.2.0.6", {"start": v(161, 45) * mm, "end": v(239, 45) * mm});
            skArc(sketch, "E122.2.0.7", {"start": v(245, 39) * mm, "mid": v(243.24, 43.24) * mm, "end": v(239, 45) * mm});
            skLineSegment(sketch, "E122.2.0.8", {"start": v(245, 39) * mm, "end": v(245, 11.88) * mm});
            skLineSegment(sketch, "E122.2.0.9", {"start": v(242.25, 39) * mm, "end": v(242.25, 16.44) * mm});
            skLineSegment(sketch, "E122.2.0.10", {"start": v(216.44, 42.25) * mm, "end": v(239, 42.25) * mm});
            skArc(sketch, "E122.2.0.11", {"start": v(242.25, 39) * mm, "mid": v(241.3, 41.3) * mm, "end": v(239, 42.25) * mm});
            skLineSegment(sketch, "E122.2.0.12", {"start": v(157.75, -10.99) * mm, "end": v(157.75, 10.99) * mm});
            skLineSegment(sketch, "E122.2.0.13", {"start": v(189.01, 42.25) * mm, "end": v(210.99, 42.25) * mm});
            skLineSegment(sketch, "E122.2.0.14", {"start": v(242.25, -16.44) * mm, "end": v(242.25, -39) * mm});
            skLineSegment(sketch, "E122.2.0.15", {"start": v(239, -42.25) * mm, "end": v(216.44, -42.25) * mm});
            skLineSegment(sketch, "E122.2.0.16", {"start": v(245, -11.88) * mm, "end": v(245, -39) * mm});
            skArc(sketch, "E122.2.0.17", {"start": v(239, -42.25) * mm, "mid": v(241.3, -41.3) * mm, "end": v(242.25, -39) * mm});
            skArc(sketch, "E122.2.0.18", {"start": v(239, -45) * mm, "mid": v(243.24, -43.24) * mm, "end": v(245, -39) * mm});
            skArc(sketch, "E122.2.0.19", {"start": v(179.47, 23) * mm, "mid": v(180.7, 23.41) * mm, "end": v(181.4, 24.48) * mm});
            skLineSegment(sketch, "E122.2.0.20", {"start": v(160.27, -14.5) * mm, "end": v(175.52, -18.6) * mm});
            skArc(sketch, "E122.2.0.21", {"start": v(161, 42.25) * mm, "mid": v(158.7, 41.3) * mm, "end": v(157.75, 39) * mm});
            skLineSegment(sketch, "E122.2.0.22", {"start": v(157.75, 10.99) * mm, "end": v(175.74, 15.8) * mm});
            skLineSegment(sketch, "E122.2.0.23", {"start": v(157.75, 16.44) * mm, "end": v(157.75, 39) * mm});
            skArc(sketch, "E122.2.0.24", {"start": v(160.27, -14.5) * mm, "mid": v(158.53, -14.85) * mm, "end": v(157.75, -16.44) * mm});
            skLineSegment(sketch, "E122.2.0.25", {"start": v(161, 42.25) * mm, "end": v(183.56, 42.25) * mm});
            skArc(sketch, "E122.2.0.26", {"start": v(180.75, 20.25) * mm, "mid": v(180.04, 19.96) * mm, "end": v(179.75, 19.25) * mm});
            skArc(sketch, "E122.2.0.27", {"start": v(161, 45) * mm, "mid": v(156.76, 43.24) * mm, "end": v(155, 39) * mm});
            skLineSegment(sketch, "E122.2.0.28", {"start": v(175.52, 18.6) * mm, "end": v(160.27, 14.5) * mm});
            skLineSegment(sketch, "E122.2.0.29", {"start": v(175.74, -15.8) * mm, "end": v(157.75, -10.99) * mm});
            skArc(sketch, "E122.2.0.30", {"start": v(157.75, 16.44) * mm, "mid": v(158.53, 14.85) * mm, "end": v(160.27, 14.5) * mm});
            skLineSegment(sketch, "E122.2.0.31", {"start": v(185.5, 39.73) * mm, "end": v(181.4, 24.48) * mm});
            skArc(sketch, "E122.2.0.32", {"start": v(181.4, -24.48) * mm, "mid": v(180.7, -23.41) * mm, "end": v(179.47, -23) * mm});
            skLineSegment(sketch, "E122.2.0.33", {"start": v(177, -9.27) * mm, "end": v(177, -14.84) * mm});
            skArc(sketch, "E122.2.0.34", {"start": v(179.7, 7.07) * mm, "mid": v(179.74, 7.23) * mm, "end": v(179.75, 7.4) * mm});
            skLineSegment(sketch, "E122.2.0.35", {"start": v(177, 21) * mm, "end": v(177, 20.53) * mm});
            skArc(sketch, "E122.2.0.36", {"start": v(209.27, -23) * mm, "mid": v(209.06, -23.02) * mm, "end": v(208.86, -23.09) * mm});
            skArc(sketch, "E122.2.0.37", {"start": v(192.93, -20.3) * mm, "mid": v(200, -21.5) * mm, "end": v(207.07, -20.3) * mm});
            skLineSegment(sketch, "E122.2.0.38", {"start": v(180.75, 20.25) * mm, "end": v(192.6, 20.25) * mm});
            skLineSegment(sketch, "E122.2.0.39", {"start": v(214.5, -39.73) * mm, "end": v(218.6, -24.48) * mm});
            skLineSegment(sketch, "E122.2.0.40", {"start": v(210.99, -42.25) * mm, "end": v(189.01, -42.25) * mm});
            skArc(sketch, "E122.2.0.41", {"start": v(179.75, -7.4) * mm, "mid": v(179.74, -7.23) * mm, "end": v(179.7, -7.07) * mm});
            skLineSegment(sketch, "E122.2.0.42", {"start": v(181.4, -24.48) * mm, "end": v(185.5, -39.73) * mm});
            skLineSegment(sketch, "E122.2.0.43", {"start": v(179.75, -19.25) * mm, "end": v(179.75, -7.4) * mm});
            skArc(sketch, "E122.2.0.44", {"start": v(192.93, -20.3) * mm, "mid": v(192.77, -20.26) * mm, "end": v(192.6, -20.25) * mm});
            skArc(sketch, "E122.2.0.45", {"start": v(176.91, 8.86) * mm, "mid": v(175, 0) * mm, "end": v(176.91, -8.86) * mm});
            skLineSegment(sketch, "E122.2.0.46", {"start": v(185.16, -23) * mm, "end": v(190.73, -23) * mm});
            skArc(sketch, "E122.2.0.47", {"start": v(220.53, -23) * mm, "mid": v(219.3, -23.41) * mm, "end": v(218.6, -24.48) * mm});
            skArc(sketch, "E122.2.0.48", {"start": v(185.16, -23) * mm, "mid": v(184.36, -23.4) * mm, "end": v(184.2, -24.26) * mm});
            skLineSegment(sketch, "E122.2.0.49", {"start": v(215.8, -24.26) * mm, "end": v(210.99, -42.25) * mm});
            skArc(sketch, "E122.2.0.50", {"start": v(175.52, 18.6) * mm, "mid": v(176.59, 19.3) * mm, "end": v(177, 20.53) * mm});
            skArc(sketch, "E122.2.0.51", {"start": v(183.56, -42.25) * mm, "mid": v(185.15, -41.47) * mm, "end": v(185.5, -39.73) * mm});
            skArc(sketch, "E122.2.0.52", {"start": v(177, -9.27) * mm, "mid": v(176.98, -9.06) * mm, "end": v(176.91, -8.86) * mm});
            skArc(sketch, "E122.2.0.53", {"start": v(207.4, -20.25) * mm, "mid": v(207.23, -20.26) * mm, "end": v(207.07, -20.3) * mm});
            skArc(sketch, "E122.2.0.54", {"start": v(179.7, 7.07) * mm, "mid": v(178.5, 0) * mm, "end": v(179.7, -7.07) * mm});
            skLineSegment(sketch, "E122.2.0.55", {"start": v(190.73, 23) * mm, "end": v(185.16, 23) * mm});
            skArc(sketch, "E122.2.0.56", {"start": v(191.14, -23.09) * mm, "mid": v(200, -25) * mm, "end": v(208.86, -23.09) * mm});
            skLineSegment(sketch, "E122.2.0.57", {"start": v(192.6, -20.25) * mm, "end": v(180.75, -20.25) * mm});
            skLineSegment(sketch, "E122.2.0.58", {"start": v(179.75, 7.4) * mm, "end": v(179.75, 19.25) * mm});
            skLineSegment(sketch, "E122.2.0.59", {"start": v(219.25, -20.25) * mm, "end": v(207.4, -20.25) * mm});
            skLineSegment(sketch, "E122.2.0.60", {"start": v(189.01, -42.25) * mm, "end": v(184.2, -24.26) * mm});
            skLineSegment(sketch, "E122.2.0.61", {"start": v(177, -20.53) * mm, "end": v(177, -21) * mm});
            skArc(sketch, "E122.2.0.62", {"start": v(214.5, -39.73) * mm, "mid": v(214.85, -41.47) * mm, "end": v(216.44, -42.25) * mm});
            skArc(sketch, "E122.2.0.63", {"start": v(191.14, -23.09) * mm, "mid": v(190.94, -23.02) * mm, "end": v(190.73, -23) * mm});
            skArc(sketch, "E122.2.0.64", {"start": v(208.86, 23.09) * mm, "mid": v(200, 25) * mm, "end": v(191.14, 23.09) * mm});
            skLineSegment(sketch, "E122.2.0.65", {"start": v(209.27, -23) * mm, "end": v(214.84, -23) * mm});
            skLineSegment(sketch, "E122.2.0.66", {"start": v(177, 14.84) * mm, "end": v(177, 9.27) * mm});
            skLineSegment(sketch, "E122.2.0.67", {"start": v(179.47, 23) * mm, "end": v(179, 23) * mm});
            skArc(sketch, "E122.2.0.68", {"start": v(215.8, -24.26) * mm, "mid": v(215.64, -23.4) * mm, "end": v(214.84, -23) * mm});
            skLineSegment(sketch, "E122.2.0.69", {"start": v(184.2, 24.26) * mm, "end": v(189.01, 42.25) * mm});
            skArc(sketch, "E122.2.0.70", {"start": v(175.74, -15.8) * mm, "mid": v(176.6, -15.64) * mm, "end": v(177, -14.84) * mm});
            skLineSegment(sketch, "E122.2.0.71", {"start": v(179, -23) * mm, "end": v(179.47, -23) * mm});
            skArc(sketch, "E122.2.0.72", {"start": v(177, 14.84) * mm, "mid": v(176.6, 15.64) * mm, "end": v(175.74, 15.8) * mm});
            skArc(sketch, "E122.2.0.73", {"start": v(184.2, 24.26) * mm, "mid": v(184.36, 23.4) * mm, "end": v(185.16, 23) * mm});
            skArc(sketch, "E122.2.0.74", {"start": v(207.07, 20.3) * mm, "mid": v(200, 21.5) * mm, "end": v(192.93, 20.3) * mm});
            skArc(sketch, "E122.2.0.75", {"start": v(177, -21) * mm, "mid": v(177.59, -22.41) * mm, "end": v(179, -23) * mm});
            skArc(sketch, "E122.2.0.76", {"start": v(192.6, 20.25) * mm, "mid": v(192.77, 20.26) * mm, "end": v(192.93, 20.3) * mm});
            skArc(sketch, "E122.2.0.77", {"start": v(179, 23) * mm, "mid": v(177.59, 22.41) * mm, "end": v(177, 21) * mm});
            skArc(sketch, "E122.2.0.78", {"start": v(179.75, -19.25) * mm, "mid": v(180.04, -19.96) * mm, "end": v(180.75, -20.25) * mm});
            skArc(sketch, "E122.2.0.79", {"start": v(190.73, 23) * mm, "mid": v(190.94, 23.02) * mm, "end": v(191.14, 23.09) * mm});
            skArc(sketch, "E122.2.0.80", {"start": v(176.91, 8.86) * mm, "mid": v(176.98, 9.06) * mm, "end": v(177, 9.27) * mm});
            skArc(sketch, "E122.2.0.81", {"start": v(177, -20.53) * mm, "mid": v(176.59, -19.3) * mm, "end": v(175.52, -18.6) * mm});
            skLineSegment(sketch, "E122.2.0.82", {"start": v(239.73, 14.5) * mm, "end": v(224.48, 18.6) * mm});
            skLineSegment(sketch, "E122.2.0.83", {"start": v(218.6, 24.48) * mm, "end": v(214.5, 39.73) * mm});
            skArc(sketch, "E122.2.0.84", {"start": v(224.26, 15.8) * mm, "mid": v(223.4, 15.64) * mm, "end": v(223, 14.84) * mm});
            skArc(sketch, "E122.2.0.85", {"start": v(219.25, -20.25) * mm, "mid": v(219.96, -19.96) * mm, "end": v(220.25, -19.25) * mm});
            skLineSegment(sketch, "E122.2.0.86", {"start": v(243.43, 10.67) * mm, "end": v(224.26, 15.8) * mm});
            skArc(sketch, "E122.2.0.87", {"start": v(185.5, 39.73) * mm, "mid": v(185.15, 41.47) * mm, "end": v(183.56, 42.25) * mm});
            skArc(sketch, "E122.2.0.88", {"start": v(223, 21) * mm, "mid": v(222.41, 22.41) * mm, "end": v(221, 23) * mm});
            skArc(sketch, "E122.2.0.89", {"start": v(239.73, 14.5) * mm, "mid": v(241.47, 14.85) * mm, "end": v(242.25, 16.44) * mm});
            skArc(sketch, "E122.2.0.90", {"start": v(223.09, -8.86) * mm, "mid": v(225, 0) * mm, "end": v(223.09, 8.86) * mm});
            skArc(sketch, "E122.2.0.91", {"start": v(220.3, -7.07) * mm, "mid": v(221.5, 0) * mm, "end": v(220.3, 7.07) * mm});
            skLineSegment(sketch, "E122.2.0.92", {"start": v(214.84, 23) * mm, "end": v(209.27, 23) * mm});
            skArc(sketch, "E122.2.0.93", {"start": v(223, 9.27) * mm, "mid": v(223.02, 9.06) * mm, "end": v(223.09, 8.86) * mm});
            skLineSegment(sketch, "E122.2.0.94", {"start": v(224.26, -15.8) * mm, "end": v(243.43, -10.67) * mm});
            skArc(sketch, "E122.2.0.95", {"start": v(242.25, -16.44) * mm, "mid": v(241.47, -14.85) * mm, "end": v(239.73, -14.5) * mm});
            skArc(sketch, "E122.2.0.96", {"start": v(223.09, -8.86) * mm, "mid": v(223.02, -9.06) * mm, "end": v(223, -9.27) * mm});
            skArc(sketch, "E122.2.0.97", {"start": v(223, -14.84) * mm, "mid": v(223.4, -15.64) * mm, "end": v(224.26, -15.8) * mm});
            skArc(sketch, "E122.2.0.98", {"start": v(216.44, 42.25) * mm, "mid": v(214.85, 41.47) * mm, "end": v(214.5, 39.73) * mm});
            skArc(sketch, "E122.2.0.99", {"start": v(245, -11.88) * mm, "mid": v(244.51, -10.89) * mm, "end": v(243.43, -10.67) * mm});
            skLineSegment(sketch, "E122.2.0.100", {"start": v(223, 20.53) * mm, "end": v(223, 21) * mm});
            skLineSegment(sketch, "E122.2.0.101", {"start": v(223, -9.27) * mm, "end": v(223, -14.84) * mm});
            skLineSegment(sketch, "E122.2.0.102", {"start": v(220.25, 19.25) * mm, "end": v(220.25, 7.4) * mm});
            skLineSegment(sketch, "E122.2.0.103", {"start": v(220.25, -7.4) * mm, "end": v(220.25, -19.25) * mm});
            skLineSegment(sketch, "E122.2.0.104", {"start": v(210.99, 42.25) * mm, "end": v(215.8, 24.26) * mm});
            skLineSegment(sketch, "E122.2.0.105", {"start": v(207.4, 20.25) * mm, "end": v(219.25, 20.25) * mm});
            skArc(sketch, "E122.2.0.106", {"start": v(243.43, 10.67) * mm, "mid": v(244.51, 10.89) * mm, "end": v(245, 11.88) * mm});
            skArc(sketch, "E122.2.0.107", {"start": v(214.84, 23) * mm, "mid": v(215.64, 23.4) * mm, "end": v(215.8, 24.26) * mm});
            skLineSegment(sketch, "E122.2.0.108", {"start": v(224.48, -18.6) * mm, "end": v(239.73, -14.5) * mm});
            skLineSegment(sketch, "E122.2.0.109", {"start": v(223, 14.84) * mm, "end": v(223, 9.27) * mm});
            skArc(sketch, "E122.2.0.110", {"start": v(218.6, 24.48) * mm, "mid": v(219.3, 23.41) * mm, "end": v(220.53, 23) * mm});
            skArc(sketch, "E122.2.0.111", {"start": v(220.25, 19.25) * mm, "mid": v(219.96, 19.96) * mm, "end": v(219.25, 20.25) * mm});
            skArc(sketch, "E122.2.0.112", {"start": v(208.86, 23.09) * mm, "mid": v(209.06, 23.02) * mm, "end": v(209.27, 23) * mm});
            skArc(sketch, "E122.2.0.113", {"start": v(220.3, -7.07) * mm, "mid": v(220.26, -7.23) * mm, "end": v(220.25, -7.4) * mm});
            skArc(sketch, "E122.2.0.114", {"start": v(221, -23) * mm, "mid": v(222.41, -22.41) * mm, "end": v(223, -21) * mm});
            skArc(sketch, "E122.2.0.115", {"start": v(207.07, 20.3) * mm, "mid": v(207.23, 20.26) * mm, "end": v(207.4, 20.25) * mm});
            skArc(sketch, "E122.2.0.116", {"start": v(220.25, 7.4) * mm, "mid": v(220.26, 7.23) * mm, "end": v(220.3, 7.07) * mm});
            skArc(sketch, "E122.2.0.117", {"start": v(223, 20.53) * mm, "mid": v(223.41, 19.3) * mm, "end": v(224.48, 18.6) * mm});
            skLineSegment(sketch, "E122.2.0.118", {"start": v(223, -21) * mm, "end": v(223, -20.53) * mm});
            skLineSegment(sketch, "E122.2.0.119", {"start": v(221, 23) * mm, "end": v(220.53, 23) * mm});
            skLineSegment(sketch, "E122.2.0.120", {"start": v(220.53, -23) * mm, "end": v(221, -23) * mm});
            skArc(sketch, "E122.2.0.121", {"start": v(224.48, -18.6) * mm, "mid": v(223.41, -19.3) * mm, "end": v(223, -20.53) * mm});
            skArc(sketch, "E122.3.0.0", {"start": v(255, -39) * mm, "mid": v(256.76, -43.24) * mm, "end": v(261, -45) * mm});
            skLineSegment(sketch, "E122.3.0.1", {"start": v(255, -39) * mm, "end": v(255, 39) * mm});
            skArc(sketch, "E122.3.0.2", {"start": v(257.75, -39) * mm, "mid": v(258.7, -41.3) * mm, "end": v(261, -42.25) * mm});
            skLineSegment(sketch, "E122.3.0.3", {"start": v(339, -45) * mm, "end": v(261, -45) * mm});
            skLineSegment(sketch, "E122.3.0.4", {"start": v(257.75, -39) * mm, "end": v(257.75, -16.44) * mm});
            skLineSegment(sketch, "E122.3.0.5", {"start": v(283.56, -42.25) * mm, "end": v(261, -42.25) * mm});
            skLineSegment(sketch, "E122.3.0.6", {"start": v(261, 45) * mm, "end": v(339, 45) * mm});
            skArc(sketch, "E122.3.0.7", {"start": v(345, 39) * mm, "mid": v(343.24, 43.24) * mm, "end": v(339, 45) * mm});
            skLineSegment(sketch, "E122.3.0.8", {"start": v(345, 39) * mm, "end": v(345, 11.88) * mm});
            skLineSegment(sketch, "E122.3.0.9", {"start": v(342.25, 39) * mm, "end": v(342.25, 16.44) * mm});
            skLineSegment(sketch, "E122.3.0.10", {"start": v(316.44, 42.25) * mm, "end": v(339, 42.25) * mm});
            skArc(sketch, "E122.3.0.11", {"start": v(342.25, 39) * mm, "mid": v(341.3, 41.3) * mm, "end": v(339, 42.25) * mm});
            skLineSegment(sketch, "E122.3.0.12", {"start": v(257.75, -10.99) * mm, "end": v(257.75, 10.99) * mm});
            skLineSegment(sketch, "E122.3.0.13", {"start": v(289.01, 42.25) * mm, "end": v(310.99, 42.25) * mm});
            skLineSegment(sketch, "E122.3.0.14", {"start": v(342.25, -16.44) * mm, "end": v(342.25, -39) * mm});
            skLineSegment(sketch, "E122.3.0.15", {"start": v(339, -42.25) * mm, "end": v(316.44, -42.25) * mm});
            skLineSegment(sketch, "E122.3.0.16", {"start": v(345, -11.88) * mm, "end": v(345, -39) * mm});
            skArc(sketch, "E122.3.0.17", {"start": v(339, -42.25) * mm, "mid": v(341.3, -41.3) * mm, "end": v(342.25, -39) * mm});
            skArc(sketch, "E122.3.0.18", {"start": v(339, -45) * mm, "mid": v(343.24, -43.24) * mm, "end": v(345, -39) * mm});
            skArc(sketch, "E122.3.0.19", {"start": v(279.47, 23) * mm, "mid": v(280.7, 23.41) * mm, "end": v(281.4, 24.48) * mm});
            skLineSegment(sketch, "E122.3.0.20", {"start": v(260.27, -14.5) * mm, "end": v(275.52, -18.6) * mm});
            skArc(sketch, "E122.3.0.21", {"start": v(261, 42.25) * mm, "mid": v(258.7, 41.3) * mm, "end": v(257.75, 39) * mm});
            skLineSegment(sketch, "E122.3.0.22", {"start": v(257.75, 10.99) * mm, "end": v(275.74, 15.8) * mm});
            skLineSegment(sketch, "E122.3.0.23", {"start": v(257.75, 16.44) * mm, "end": v(257.75, 39) * mm});
            skArc(sketch, "E122.3.0.24", {"start": v(260.27, -14.5) * mm, "mid": v(258.53, -14.85) * mm, "end": v(257.75, -16.44) * mm});
            skLineSegment(sketch, "E122.3.0.25", {"start": v(261, 42.25) * mm, "end": v(283.56, 42.25) * mm});
            skArc(sketch, "E122.3.0.26", {"start": v(280.75, 20.25) * mm, "mid": v(280.04, 19.96) * mm, "end": v(279.75, 19.25) * mm});
            skArc(sketch, "E122.3.0.27", {"start": v(261, 45) * mm, "mid": v(256.76, 43.24) * mm, "end": v(255, 39) * mm});
            skLineSegment(sketch, "E122.3.0.28", {"start": v(275.52, 18.6) * mm, "end": v(260.27, 14.5) * mm});
            skLineSegment(sketch, "E122.3.0.29", {"start": v(275.74, -15.8) * mm, "end": v(257.75, -10.99) * mm});
            skArc(sketch, "E122.3.0.30", {"start": v(257.75, 16.44) * mm, "mid": v(258.53, 14.85) * mm, "end": v(260.27, 14.5) * mm});
            skLineSegment(sketch, "E122.3.0.31", {"start": v(285.5, 39.73) * mm, "end": v(281.4, 24.48) * mm});
            skArc(sketch, "E122.3.0.32", {"start": v(281.4, -24.48) * mm, "mid": v(280.7, -23.41) * mm, "end": v(279.47, -23) * mm});
            skLineSegment(sketch, "E122.3.0.33", {"start": v(277, -9.27) * mm, "end": v(277, -14.84) * mm});
            skArc(sketch, "E122.3.0.34", {"start": v(279.7, 7.07) * mm, "mid": v(279.74, 7.23) * mm, "end": v(279.75, 7.4) * mm});
            skLineSegment(sketch, "E122.3.0.35", {"start": v(277, 21) * mm, "end": v(277, 20.53) * mm});
            skArc(sketch, "E122.3.0.36", {"start": v(309.27, -23) * mm, "mid": v(309.06, -23.02) * mm, "end": v(308.86, -23.09) * mm});
            skArc(sketch, "E122.3.0.37", {"start": v(292.93, -20.3) * mm, "mid": v(300, -21.5) * mm, "end": v(307.07, -20.3) * mm});
            skLineSegment(sketch, "E122.3.0.38", {"start": v(280.75, 20.25) * mm, "end": v(292.6, 20.25) * mm});
            skLineSegment(sketch, "E122.3.0.39", {"start": v(314.5, -39.73) * mm, "end": v(318.6, -24.48) * mm});
            skLineSegment(sketch, "E122.3.0.40", {"start": v(310.99, -42.25) * mm, "end": v(289.01, -42.25) * mm});
            skArc(sketch, "E122.3.0.41", {"start": v(279.75, -7.4) * mm, "mid": v(279.74, -7.23) * mm, "end": v(279.7, -7.07) * mm});
            skLineSegment(sketch, "E122.3.0.42", {"start": v(281.4, -24.48) * mm, "end": v(285.5, -39.73) * mm});
            skLineSegment(sketch, "E122.3.0.43", {"start": v(279.75, -19.25) * mm, "end": v(279.75, -7.4) * mm});
            skArc(sketch, "E122.3.0.44", {"start": v(292.93, -20.3) * mm, "mid": v(292.77, -20.26) * mm, "end": v(292.6, -20.25) * mm});
            skArc(sketch, "E122.3.0.45", {"start": v(276.91, 8.86) * mm, "mid": v(275, 0) * mm, "end": v(276.91, -8.86) * mm});
            skLineSegment(sketch, "E122.3.0.46", {"start": v(285.16, -23) * mm, "end": v(290.73, -23) * mm});
            skArc(sketch, "E122.3.0.47", {"start": v(320.53, -23) * mm, "mid": v(319.3, -23.41) * mm, "end": v(318.6, -24.48) * mm});
            skArc(sketch, "E122.3.0.48", {"start": v(285.16, -23) * mm, "mid": v(284.36, -23.4) * mm, "end": v(284.2, -24.26) * mm});
            skLineSegment(sketch, "E122.3.0.49", {"start": v(315.8, -24.26) * mm, "end": v(310.99, -42.25) * mm});
            skArc(sketch, "E122.3.0.50", {"start": v(275.52, 18.6) * mm, "mid": v(276.59, 19.3) * mm, "end": v(277, 20.53) * mm});
            skArc(sketch, "E122.3.0.51", {"start": v(283.56, -42.25) * mm, "mid": v(285.15, -41.47) * mm, "end": v(285.5, -39.73) * mm});
            skArc(sketch, "E122.3.0.52", {"start": v(277, -9.27) * mm, "mid": v(276.98, -9.06) * mm, "end": v(276.91, -8.86) * mm});
            skArc(sketch, "E122.3.0.53", {"start": v(307.4, -20.25) * mm, "mid": v(307.23, -20.26) * mm, "end": v(307.07, -20.3) * mm});
            skArc(sketch, "E122.3.0.54", {"start": v(279.7, 7.07) * mm, "mid": v(278.5, 0) * mm, "end": v(279.7, -7.07) * mm});
            skLineSegment(sketch, "E122.3.0.55", {"start": v(290.73, 23) * mm, "end": v(285.16, 23) * mm});
            skArc(sketch, "E122.3.0.56", {"start": v(291.14, -23.09) * mm, "mid": v(300, -25) * mm, "end": v(308.86, -23.09) * mm});
            skLineSegment(sketch, "E122.3.0.57", {"start": v(292.6, -20.25) * mm, "end": v(280.75, -20.25) * mm});
            skLineSegment(sketch, "E122.3.0.58", {"start": v(279.75, 7.4) * mm, "end": v(279.75, 19.25) * mm});
            skLineSegment(sketch, "E122.3.0.59", {"start": v(319.25, -20.25) * mm, "end": v(307.4, -20.25) * mm});
            skLineSegment(sketch, "E122.3.0.60", {"start": v(289.01, -42.25) * mm, "end": v(284.2, -24.26) * mm});
            skLineSegment(sketch, "E122.3.0.61", {"start": v(277, -20.53) * mm, "end": v(277, -21) * mm});
            skArc(sketch, "E122.3.0.62", {"start": v(314.5, -39.73) * mm, "mid": v(314.85, -41.47) * mm, "end": v(316.44, -42.25) * mm});
            skArc(sketch, "E122.3.0.63", {"start": v(291.14, -23.09) * mm, "mid": v(290.94, -23.02) * mm, "end": v(290.73, -23) * mm});
            skArc(sketch, "E122.3.0.64", {"start": v(308.86, 23.09) * mm, "mid": v(300, 25) * mm, "end": v(291.14, 23.09) * mm});
            skLineSegment(sketch, "E122.3.0.65", {"start": v(309.27, -23) * mm, "end": v(314.84, -23) * mm});
            skLineSegment(sketch, "E122.3.0.66", {"start": v(277, 14.84) * mm, "end": v(277, 9.27) * mm});
            skLineSegment(sketch, "E122.3.0.67", {"start": v(279.47, 23) * mm, "end": v(279, 23) * mm});
            skArc(sketch, "E122.3.0.68", {"start": v(315.8, -24.26) * mm, "mid": v(315.64, -23.4) * mm, "end": v(314.84, -23) * mm});
            skLineSegment(sketch, "E122.3.0.69", {"start": v(284.2, 24.26) * mm, "end": v(289.01, 42.25) * mm});
            skArc(sketch, "E122.3.0.70", {"start": v(275.74, -15.8) * mm, "mid": v(276.6, -15.64) * mm, "end": v(277, -14.84) * mm});
            skLineSegment(sketch, "E122.3.0.71", {"start": v(279, -23) * mm, "end": v(279.47, -23) * mm});
            skArc(sketch, "E122.3.0.72", {"start": v(277, 14.84) * mm, "mid": v(276.6, 15.64) * mm, "end": v(275.74, 15.8) * mm});
            skArc(sketch, "E122.3.0.73", {"start": v(284.2, 24.26) * mm, "mid": v(284.36, 23.4) * mm, "end": v(285.16, 23) * mm});
            skArc(sketch, "E122.3.0.74", {"start": v(307.07, 20.3) * mm, "mid": v(300, 21.5) * mm, "end": v(292.93, 20.3) * mm});
            skArc(sketch, "E122.3.0.75", {"start": v(277, -21) * mm, "mid": v(277.59, -22.41) * mm, "end": v(279, -23) * mm});
            skArc(sketch, "E122.3.0.76", {"start": v(292.6, 20.25) * mm, "mid": v(292.77, 20.26) * mm, "end": v(292.93, 20.3) * mm});
            skArc(sketch, "E122.3.0.77", {"start": v(279, 23) * mm, "mid": v(277.59, 22.41) * mm, "end": v(277, 21) * mm});
            skArc(sketch, "E122.3.0.78", {"start": v(279.75, -19.25) * mm, "mid": v(280.04, -19.96) * mm, "end": v(280.75, -20.25) * mm});
            skArc(sketch, "E122.3.0.79", {"start": v(290.73, 23) * mm, "mid": v(290.94, 23.02) * mm, "end": v(291.14, 23.09) * mm});
            skArc(sketch, "E122.3.0.80", {"start": v(276.91, 8.86) * mm, "mid": v(276.98, 9.06) * mm, "end": v(277, 9.27) * mm});
            skArc(sketch, "E122.3.0.81", {"start": v(277, -20.53) * mm, "mid": v(276.59, -19.3) * mm, "end": v(275.52, -18.6) * mm});
            skLineSegment(sketch, "E122.3.0.82", {"start": v(339.73, 14.5) * mm, "end": v(324.48, 18.6) * mm});
            skLineSegment(sketch, "E122.3.0.83", {"start": v(318.6, 24.48) * mm, "end": v(314.5, 39.73) * mm});
            skArc(sketch, "E122.3.0.84", {"start": v(324.26, 15.8) * mm, "mid": v(323.4, 15.64) * mm, "end": v(323, 14.84) * mm});
            skArc(sketch, "E122.3.0.85", {"start": v(319.25, -20.25) * mm, "mid": v(319.96, -19.96) * mm, "end": v(320.25, -19.25) * mm});
            skLineSegment(sketch, "E122.3.0.86", {"start": v(343.43, 10.67) * mm, "end": v(324.26, 15.8) * mm});
            skArc(sketch, "E122.3.0.87", {"start": v(285.5, 39.73) * mm, "mid": v(285.15, 41.47) * mm, "end": v(283.56, 42.25) * mm});
            skArc(sketch, "E122.3.0.88", {"start": v(323, 21) * mm, "mid": v(322.41, 22.41) * mm, "end": v(321, 23) * mm});
            skArc(sketch, "E122.3.0.89", {"start": v(339.73, 14.5) * mm, "mid": v(341.47, 14.85) * mm, "end": v(342.25, 16.44) * mm});
            skArc(sketch, "E122.3.0.90", {"start": v(323.09, -8.86) * mm, "mid": v(325, 0) * mm, "end": v(323.09, 8.86) * mm});
            skArc(sketch, "E122.3.0.91", {"start": v(320.3, -7.07) * mm, "mid": v(321.5, 0) * mm, "end": v(320.3, 7.07) * mm});
            skLineSegment(sketch, "E122.3.0.92", {"start": v(314.84, 23) * mm, "end": v(309.27, 23) * mm});
            skArc(sketch, "E122.3.0.93", {"start": v(323, 9.27) * mm, "mid": v(323.02, 9.06) * mm, "end": v(323.09, 8.86) * mm});
            skLineSegment(sketch, "E122.3.0.94", {"start": v(324.26, -15.8) * mm, "end": v(343.43, -10.67) * mm});
            skArc(sketch, "E122.3.0.95", {"start": v(342.25, -16.44) * mm, "mid": v(341.47, -14.85) * mm, "end": v(339.73, -14.5) * mm});
            skArc(sketch, "E122.3.0.96", {"start": v(323.09, -8.86) * mm, "mid": v(323.02, -9.06) * mm, "end": v(323, -9.27) * mm});
            skArc(sketch, "E122.3.0.97", {"start": v(323, -14.84) * mm, "mid": v(323.4, -15.64) * mm, "end": v(324.26, -15.8) * mm});
            skArc(sketch, "E122.3.0.98", {"start": v(316.44, 42.25) * mm, "mid": v(314.85, 41.47) * mm, "end": v(314.5, 39.73) * mm});
            skArc(sketch, "E122.3.0.99", {"start": v(345, -11.88) * mm, "mid": v(344.51, -10.89) * mm, "end": v(343.43, -10.67) * mm});
            skLineSegment(sketch, "E122.3.0.100", {"start": v(323, 20.53) * mm, "end": v(323, 21) * mm});
            skLineSegment(sketch, "E122.3.0.101", {"start": v(323, -9.27) * mm, "end": v(323, -14.84) * mm});
            skLineSegment(sketch, "E122.3.0.102", {"start": v(320.25, 19.25) * mm, "end": v(320.25, 7.4) * mm});
            skLineSegment(sketch, "E122.3.0.103", {"start": v(320.25, -7.4) * mm, "end": v(320.25, -19.25) * mm});
            skLineSegment(sketch, "E122.3.0.104", {"start": v(310.99, 42.25) * mm, "end": v(315.8, 24.26) * mm});
            skLineSegment(sketch, "E122.3.0.105", {"start": v(307.4, 20.25) * mm, "end": v(319.25, 20.25) * mm});
            skArc(sketch, "E122.3.0.106", {"start": v(343.43, 10.67) * mm, "mid": v(344.51, 10.89) * mm, "end": v(345, 11.88) * mm});
            skArc(sketch, "E122.3.0.107", {"start": v(314.84, 23) * mm, "mid": v(315.64, 23.4) * mm, "end": v(315.8, 24.26) * mm});
            skLineSegment(sketch, "E122.3.0.108", {"start": v(324.48, -18.6) * mm, "end": v(339.73, -14.5) * mm});
            skLineSegment(sketch, "E122.3.0.109", {"start": v(323, 14.84) * mm, "end": v(323, 9.27) * mm});
            skArc(sketch, "E122.3.0.110", {"start": v(318.6, 24.48) * mm, "mid": v(319.3, 23.41) * mm, "end": v(320.53, 23) * mm});
            skArc(sketch, "E122.3.0.111", {"start": v(320.25, 19.25) * mm, "mid": v(319.96, 19.96) * mm, "end": v(319.25, 20.25) * mm});
            skArc(sketch, "E122.3.0.112", {"start": v(308.86, 23.09) * mm, "mid": v(309.06, 23.02) * mm, "end": v(309.27, 23) * mm});
            skArc(sketch, "E122.3.0.113", {"start": v(320.3, -7.07) * mm, "mid": v(320.26, -7.23) * mm, "end": v(320.25, -7.4) * mm});
            skArc(sketch, "E122.3.0.114", {"start": v(321, -23) * mm, "mid": v(322.41, -22.41) * mm, "end": v(323, -21) * mm});
            skArc(sketch, "E122.3.0.115", {"start": v(307.07, 20.3) * mm, "mid": v(307.23, 20.26) * mm, "end": v(307.4, 20.25) * mm});
            skArc(sketch, "E122.3.0.116", {"start": v(320.25, 7.4) * mm, "mid": v(320.26, 7.23) * mm, "end": v(320.3, 7.07) * mm});
            skArc(sketch, "E122.3.0.117", {"start": v(323, 20.53) * mm, "mid": v(323.41, 19.3) * mm, "end": v(324.48, 18.6) * mm});
            skLineSegment(sketch, "E122.3.0.118", {"start": v(323, -21) * mm, "end": v(323, -20.53) * mm});
            skLineSegment(sketch, "E122.3.0.119", {"start": v(321, 23) * mm, "end": v(320.53, 23) * mm});
            skLineSegment(sketch, "E122.3.0.120", {"start": v(320.53, -23) * mm, "end": v(321, -23) * mm});
            skArc(sketch, "E122.3.0.121", {"start": v(324.48, -18.6) * mm, "mid": v(323.41, -19.3) * mm, "end": v(323, -20.53) * mm});
            skArc(sketch, "E122.4.0.0", {"start": v(355, -39) * mm, "mid": v(356.76, -43.24) * mm, "end": v(361, -45) * mm});
            skLineSegment(sketch, "E122.4.0.1", {"start": v(355, -39) * mm, "end": v(355, 39) * mm});
            skArc(sketch, "E122.4.0.2", {"start": v(357.75, -39) * mm, "mid": v(358.7, -41.3) * mm, "end": v(361, -42.25) * mm});
            skLineSegment(sketch, "E122.4.0.3", {"start": v(439, -45) * mm, "end": v(361, -45) * mm});
            skLineSegment(sketch, "E122.4.0.4", {"start": v(357.75, -39) * mm, "end": v(357.75, -16.44) * mm});
            skLineSegment(sketch, "E122.4.0.5", {"start": v(383.56, -42.25) * mm, "end": v(361, -42.25) * mm});
            skLineSegment(sketch, "E122.4.0.6", {"start": v(361, 45) * mm, "end": v(439, 45) * mm});
            skArc(sketch, "E122.4.0.7", {"start": v(445, 39) * mm, "mid": v(443.24, 43.24) * mm, "end": v(439, 45) * mm});
            skLineSegment(sketch, "E122.4.0.8", {"start": v(445, 39) * mm, "end": v(445, 11.88) * mm});
            skLineSegment(sketch, "E122.4.0.9", {"start": v(442.25, 39) * mm, "end": v(442.25, 16.44) * mm});
            skLineSegment(sketch, "E122.4.0.10", {"start": v(416.44, 42.25) * mm, "end": v(439, 42.25) * mm});
            skArc(sketch, "E122.4.0.11", {"start": v(442.25, 39) * mm, "mid": v(441.3, 41.3) * mm, "end": v(439, 42.25) * mm});
            skLineSegment(sketch, "E122.4.0.12", {"start": v(357.75, -10.99) * mm, "end": v(357.75, 10.99) * mm});
            skLineSegment(sketch, "E122.4.0.13", {"start": v(389.01, 42.25) * mm, "end": v(410.99, 42.25) * mm});
            skLineSegment(sketch, "E122.4.0.14", {"start": v(442.25, -16.44) * mm, "end": v(442.25, -39) * mm});
            skLineSegment(sketch, "E122.4.0.15", {"start": v(439, -42.25) * mm, "end": v(416.44, -42.25) * mm});
            skLineSegment(sketch, "E122.4.0.16", {"start": v(445, -11.88) * mm, "end": v(445, -39) * mm});
            skArc(sketch, "E122.4.0.17", {"start": v(439, -42.25) * mm, "mid": v(441.3, -41.3) * mm, "end": v(442.25, -39) * mm});
            skArc(sketch, "E122.4.0.18", {"start": v(439, -45) * mm, "mid": v(443.24, -43.24) * mm, "end": v(445, -39) * mm});
            skArc(sketch, "E122.4.0.19", {"start": v(379.47, 23) * mm, "mid": v(380.7, 23.41) * mm, "end": v(381.4, 24.48) * mm});
            skLineSegment(sketch, "E122.4.0.20", {"start": v(360.27, -14.5) * mm, "end": v(375.52, -18.6) * mm});
            skArc(sketch, "E122.4.0.21", {"start": v(361, 42.25) * mm, "mid": v(358.7, 41.3) * mm, "end": v(357.75, 39) * mm});
            skLineSegment(sketch, "E122.4.0.22", {"start": v(357.75, 10.99) * mm, "end": v(375.74, 15.8) * mm});
            skLineSegment(sketch, "E122.4.0.23", {"start": v(357.75, 16.44) * mm, "end": v(357.75, 39) * mm});
            skArc(sketch, "E122.4.0.24", {"start": v(360.27, -14.5) * mm, "mid": v(358.53, -14.85) * mm, "end": v(357.75, -16.44) * mm});
            skLineSegment(sketch, "E122.4.0.25", {"start": v(361, 42.25) * mm, "end": v(383.56, 42.25) * mm});
            skArc(sketch, "E122.4.0.26", {"start": v(380.75, 20.25) * mm, "mid": v(380.04, 19.96) * mm, "end": v(379.75, 19.25) * mm});
            skArc(sketch, "E122.4.0.27", {"start": v(361, 45) * mm, "mid": v(356.76, 43.24) * mm, "end": v(355, 39) * mm});
            skLineSegment(sketch, "E122.4.0.28", {"start": v(375.52, 18.6) * mm, "end": v(360.27, 14.5) * mm});
            skLineSegment(sketch, "E122.4.0.29", {"start": v(375.74, -15.8) * mm, "end": v(357.75, -10.99) * mm});
            skArc(sketch, "E122.4.0.30", {"start": v(357.75, 16.44) * mm, "mid": v(358.53, 14.85) * mm, "end": v(360.27, 14.5) * mm});
            skLineSegment(sketch, "E122.4.0.31", {"start": v(385.5, 39.73) * mm, "end": v(381.4, 24.48) * mm});
            skArc(sketch, "E122.4.0.32", {"start": v(381.4, -24.48) * mm, "mid": v(380.7, -23.41) * mm, "end": v(379.47, -23) * mm});
            skLineSegment(sketch, "E122.4.0.33", {"start": v(377, -9.27) * mm, "end": v(377, -14.84) * mm});
            skArc(sketch, "E122.4.0.34", {"start": v(379.7, 7.07) * mm, "mid": v(379.74, 7.23) * mm, "end": v(379.75, 7.4) * mm});
            skLineSegment(sketch, "E122.4.0.35", {"start": v(377, 21) * mm, "end": v(377, 20.53) * mm});
            skArc(sketch, "E122.4.0.36", {"start": v(409.27, -23) * mm, "mid": v(409.06, -23.02) * mm, "end": v(408.86, -23.09) * mm});
            skArc(sketch, "E122.4.0.37", {"start": v(392.93, -20.3) * mm, "mid": v(400, -21.5) * mm, "end": v(407.07, -20.3) * mm});
            skLineSegment(sketch, "E122.4.0.38", {"start": v(380.75, 20.25) * mm, "end": v(392.6, 20.25) * mm});
            skLineSegment(sketch, "E122.4.0.39", {"start": v(414.5, -39.73) * mm, "end": v(418.6, -24.48) * mm});
            skLineSegment(sketch, "E122.4.0.40", {"start": v(410.99, -42.25) * mm, "end": v(389.01, -42.25) * mm});
            skArc(sketch, "E122.4.0.41", {"start": v(379.75, -7.4) * mm, "mid": v(379.74, -7.23) * mm, "end": v(379.7, -7.07) * mm});
            skLineSegment(sketch, "E122.4.0.42", {"start": v(381.4, -24.48) * mm, "end": v(385.5, -39.73) * mm});
            skLineSegment(sketch, "E122.4.0.43", {"start": v(379.75, -19.25) * mm, "end": v(379.75, -7.4) * mm});
            skArc(sketch, "E122.4.0.44", {"start": v(392.93, -20.3) * mm, "mid": v(392.77, -20.26) * mm, "end": v(392.6, -20.25) * mm});
            skArc(sketch, "E122.4.0.45", {"start": v(376.91, 8.86) * mm, "mid": v(375, 0) * mm, "end": v(376.91, -8.86) * mm});
            skLineSegment(sketch, "E122.4.0.46", {"start": v(385.16, -23) * mm, "end": v(390.73, -23) * mm});
            skArc(sketch, "E122.4.0.47", {"start": v(420.53, -23) * mm, "mid": v(419.3, -23.41) * mm, "end": v(418.6, -24.48) * mm});
            skArc(sketch, "E122.4.0.48", {"start": v(385.16, -23) * mm, "mid": v(384.36, -23.4) * mm, "end": v(384.2, -24.26) * mm});
            skLineSegment(sketch, "E122.4.0.49", {"start": v(415.8, -24.26) * mm, "end": v(410.99, -42.25) * mm});
            skArc(sketch, "E122.4.0.50", {"start": v(375.52, 18.6) * mm, "mid": v(376.59, 19.3) * mm, "end": v(377, 20.53) * mm});
            skArc(sketch, "E122.4.0.51", {"start": v(383.56, -42.25) * mm, "mid": v(385.15, -41.47) * mm, "end": v(385.5, -39.73) * mm});
            skArc(sketch, "E122.4.0.52", {"start": v(377, -9.27) * mm, "mid": v(376.98, -9.06) * mm, "end": v(376.91, -8.86) * mm});
            skArc(sketch, "E122.4.0.53", {"start": v(407.4, -20.25) * mm, "mid": v(407.23, -20.26) * mm, "end": v(407.07, -20.3) * mm});
            skArc(sketch, "E122.4.0.54", {"start": v(379.7, 7.07) * mm, "mid": v(378.5, 0) * mm, "end": v(379.7, -7.07) * mm});
            skLineSegment(sketch, "E122.4.0.55", {"start": v(390.73, 23) * mm, "end": v(385.16, 23) * mm});
            skArc(sketch, "E122.4.0.56", {"start": v(391.14, -23.09) * mm, "mid": v(400, -25) * mm, "end": v(408.86, -23.09) * mm});
            skLineSegment(sketch, "E122.4.0.57", {"start": v(392.6, -20.25) * mm, "end": v(380.75, -20.25) * mm});
            skLineSegment(sketch, "E122.4.0.58", {"start": v(379.75, 7.4) * mm, "end": v(379.75, 19.25) * mm});
            skLineSegment(sketch, "E122.4.0.59", {"start": v(419.25, -20.25) * mm, "end": v(407.4, -20.25) * mm});
            skLineSegment(sketch, "E122.4.0.60", {"start": v(389.01, -42.25) * mm, "end": v(384.2, -24.26) * mm});
            skLineSegment(sketch, "E122.4.0.61", {"start": v(377, -20.53) * mm, "end": v(377, -21) * mm});
            skArc(sketch, "E122.4.0.62", {"start": v(414.5, -39.73) * mm, "mid": v(414.85, -41.47) * mm, "end": v(416.44, -42.25) * mm});
            skArc(sketch, "E122.4.0.63", {"start": v(391.14, -23.09) * mm, "mid": v(390.94, -23.02) * mm, "end": v(390.73, -23) * mm});
            skArc(sketch, "E122.4.0.64", {"start": v(408.86, 23.09) * mm, "mid": v(400, 25) * mm, "end": v(391.14, 23.09) * mm});
            skLineSegment(sketch, "E122.4.0.65", {"start": v(409.27, -23) * mm, "end": v(414.84, -23) * mm});
            skLineSegment(sketch, "E122.4.0.66", {"start": v(377, 14.84) * mm, "end": v(377, 9.27) * mm});
            skLineSegment(sketch, "E122.4.0.67", {"start": v(379.47, 23) * mm, "end": v(379, 23) * mm});
            skArc(sketch, "E122.4.0.68", {"start": v(415.8, -24.26) * mm, "mid": v(415.64, -23.4) * mm, "end": v(414.84, -23) * mm});
            skLineSegment(sketch, "E122.4.0.69", {"start": v(384.2, 24.26) * mm, "end": v(389.01, 42.25) * mm});
            skArc(sketch, "E122.4.0.70", {"start": v(375.74, -15.8) * mm, "mid": v(376.6, -15.64) * mm, "end": v(377, -14.84) * mm});
            skLineSegment(sketch, "E122.4.0.71", {"start": v(379, -23) * mm, "end": v(379.47, -23) * mm});
            skArc(sketch, "E122.4.0.72", {"start": v(377, 14.84) * mm, "mid": v(376.6, 15.64) * mm, "end": v(375.74, 15.8) * mm});
            skArc(sketch, "E122.4.0.73", {"start": v(384.2, 24.26) * mm, "mid": v(384.36, 23.4) * mm, "end": v(385.16, 23) * mm});
            skArc(sketch, "E122.4.0.74", {"start": v(407.07, 20.3) * mm, "mid": v(400, 21.5) * mm, "end": v(392.93, 20.3) * mm});
            skArc(sketch, "E122.4.0.75", {"start": v(377, -21) * mm, "mid": v(377.59, -22.41) * mm, "end": v(379, -23) * mm});
            skArc(sketch, "E122.4.0.76", {"start": v(392.6, 20.25) * mm, "mid": v(392.77, 20.26) * mm, "end": v(392.93, 20.3) * mm});
            skArc(sketch, "E122.4.0.77", {"start": v(379, 23) * mm, "mid": v(377.59, 22.41) * mm, "end": v(377, 21) * mm});
            skArc(sketch, "E122.4.0.78", {"start": v(379.75, -19.25) * mm, "mid": v(380.04, -19.96) * mm, "end": v(380.75, -20.25) * mm});
            skArc(sketch, "E122.4.0.79", {"start": v(390.73, 23) * mm, "mid": v(390.94, 23.02) * mm, "end": v(391.14, 23.09) * mm});
            skArc(sketch, "E122.4.0.80", {"start": v(376.91, 8.86) * mm, "mid": v(376.98, 9.06) * mm, "end": v(377, 9.27) * mm});
            skArc(sketch, "E122.4.0.81", {"start": v(377, -20.53) * mm, "mid": v(376.59, -19.3) * mm, "end": v(375.52, -18.6) * mm});
            skLineSegment(sketch, "E122.4.0.82", {"start": v(439.73, 14.5) * mm, "end": v(424.48, 18.6) * mm});
            skLineSegment(sketch, "E122.4.0.83", {"start": v(418.6, 24.48) * mm, "end": v(414.5, 39.73) * mm});
            skArc(sketch, "E122.4.0.84", {"start": v(424.26, 15.8) * mm, "mid": v(423.4, 15.64) * mm, "end": v(423, 14.84) * mm});
            skArc(sketch, "E122.4.0.85", {"start": v(419.25, -20.25) * mm, "mid": v(419.96, -19.96) * mm, "end": v(420.25, -19.25) * mm});
            skLineSegment(sketch, "E122.4.0.86", {"start": v(443.43, 10.67) * mm, "end": v(424.26, 15.8) * mm});
            skArc(sketch, "E122.4.0.87", {"start": v(385.5, 39.73) * mm, "mid": v(385.15, 41.47) * mm, "end": v(383.56, 42.25) * mm});
            skArc(sketch, "E122.4.0.88", {"start": v(423, 21) * mm, "mid": v(422.41, 22.41) * mm, "end": v(421, 23) * mm});
            skArc(sketch, "E122.4.0.89", {"start": v(439.73, 14.5) * mm, "mid": v(441.47, 14.85) * mm, "end": v(442.25, 16.44) * mm});
            skArc(sketch, "E122.4.0.90", {"start": v(423.09, -8.86) * mm, "mid": v(425, 0) * mm, "end": v(423.09, 8.86) * mm});
            skArc(sketch, "E122.4.0.91", {"start": v(420.3, -7.07) * mm, "mid": v(421.5, 0) * mm, "end": v(420.3, 7.07) * mm});
            skLineSegment(sketch, "E122.4.0.92", {"start": v(414.84, 23) * mm, "end": v(409.27, 23) * mm});
            skArc(sketch, "E122.4.0.93", {"start": v(423, 9.27) * mm, "mid": v(423.02, 9.06) * mm, "end": v(423.09, 8.86) * mm});
            skLineSegment(sketch, "E122.4.0.94", {"start": v(424.26, -15.8) * mm, "end": v(443.43, -10.67) * mm});
            skArc(sketch, "E122.4.0.95", {"start": v(442.25, -16.44) * mm, "mid": v(441.47, -14.85) * mm, "end": v(439.73, -14.5) * mm});
            skArc(sketch, "E122.4.0.96", {"start": v(423.09, -8.86) * mm, "mid": v(423.02, -9.06) * mm, "end": v(423, -9.27) * mm});
            skArc(sketch, "E122.4.0.97", {"start": v(423, -14.84) * mm, "mid": v(423.4, -15.64) * mm, "end": v(424.26, -15.8) * mm});
            skArc(sketch, "E122.4.0.98", {"start": v(416.44, 42.25) * mm, "mid": v(414.85, 41.47) * mm, "end": v(414.5, 39.73) * mm});
            skArc(sketch, "E122.4.0.99", {"start": v(445, -11.88) * mm, "mid": v(444.51, -10.89) * mm, "end": v(443.43, -10.67) * mm});
            skLineSegment(sketch, "E122.4.0.100", {"start": v(423, 20.53) * mm, "end": v(423, 21) * mm});
            skLineSegment(sketch, "E122.4.0.101", {"start": v(423, -9.27) * mm, "end": v(423, -14.84) * mm});
            skLineSegment(sketch, "E122.4.0.102", {"start": v(420.25, 19.25) * mm, "end": v(420.25, 7.4) * mm});
            skLineSegment(sketch, "E122.4.0.103", {"start": v(420.25, -7.4) * mm, "end": v(420.25, -19.25) * mm});
            skLineSegment(sketch, "E122.4.0.104", {"start": v(410.99, 42.25) * mm, "end": v(415.8, 24.26) * mm});
            skLineSegment(sketch, "E122.4.0.105", {"start": v(407.4, 20.25) * mm, "end": v(419.25, 20.25) * mm});
            skArc(sketch, "E122.4.0.106", {"start": v(443.43, 10.67) * mm, "mid": v(444.51, 10.89) * mm, "end": v(445, 11.88) * mm});
            skArc(sketch, "E122.4.0.107", {"start": v(414.84, 23) * mm, "mid": v(415.64, 23.4) * mm, "end": v(415.8, 24.26) * mm});
            skLineSegment(sketch, "E122.4.0.108", {"start": v(424.48, -18.6) * mm, "end": v(439.73, -14.5) * mm});
            skLineSegment(sketch, "E122.4.0.109", {"start": v(423, 14.84) * mm, "end": v(423, 9.27) * mm});
            skArc(sketch, "E122.4.0.110", {"start": v(418.6, 24.48) * mm, "mid": v(419.3, 23.41) * mm, "end": v(420.53, 23) * mm});
            skArc(sketch, "E122.4.0.111", {"start": v(420.25, 19.25) * mm, "mid": v(419.96, 19.96) * mm, "end": v(419.25, 20.25) * mm});
            skArc(sketch, "E122.4.0.112", {"start": v(408.86, 23.09) * mm, "mid": v(409.06, 23.02) * mm, "end": v(409.27, 23) * mm});
            skArc(sketch, "E122.4.0.113", {"start": v(420.3, -7.07) * mm, "mid": v(420.26, -7.23) * mm, "end": v(420.25, -7.4) * mm});
            skArc(sketch, "E122.4.0.114", {"start": v(421, -23) * mm, "mid": v(422.41, -22.41) * mm, "end": v(423, -21) * mm});
            skArc(sketch, "E122.4.0.115", {"start": v(407.07, 20.3) * mm, "mid": v(407.23, 20.26) * mm, "end": v(407.4, 20.25) * mm});
            skArc(sketch, "E122.4.0.116", {"start": v(420.25, 7.4) * mm, "mid": v(420.26, 7.23) * mm, "end": v(420.3, 7.07) * mm});
            skArc(sketch, "E122.4.0.117", {"start": v(423, 20.53) * mm, "mid": v(423.41, 19.3) * mm, "end": v(424.48, 18.6) * mm});
            skLineSegment(sketch, "E122.4.0.118", {"start": v(423, -21) * mm, "end": v(423, -20.53) * mm});
            skLineSegment(sketch, "E122.4.0.119", {"start": v(421, 23) * mm, "end": v(420.53, 23) * mm});
            skLineSegment(sketch, "E122.4.0.120", {"start": v(420.53, -23) * mm, "end": v(421, -23) * mm});
            skArc(sketch, "E122.4.0.121", {"start": v(424.48, -18.6) * mm, "mid": v(423.41, -19.3) * mm, "end": v(423, -20.53) * mm});
            skArc(sketch, "E122.5.0.0", {"start": v(455, -39) * mm, "mid": v(456.76, -43.24) * mm, "end": v(461, -45) * mm});
            skLineSegment(sketch, "E122.5.0.1", {"start": v(455, -39) * mm, "end": v(455, 39) * mm});
            skArc(sketch, "E122.5.0.2", {"start": v(457.75, -39) * mm, "mid": v(458.7, -41.3) * mm, "end": v(461, -42.25) * mm});
            skLineSegment(sketch, "E122.5.0.3", {"start": v(539, -45) * mm, "end": v(461, -45) * mm});
            skLineSegment(sketch, "E122.5.0.4", {"start": v(457.75, -39) * mm, "end": v(457.75, -16.44) * mm});
            skLineSegment(sketch, "E122.5.0.5", {"start": v(483.56, -42.25) * mm, "end": v(461, -42.25) * mm});
            skLineSegment(sketch, "E122.5.0.6", {"start": v(461, 45) * mm, "end": v(539, 45) * mm});
            skArc(sketch, "E122.5.0.7", {"start": v(545, 39) * mm, "mid": v(543.24, 43.24) * mm, "end": v(539, 45) * mm});
            skLineSegment(sketch, "E122.5.0.8", {"start": v(545, 39) * mm, "end": v(545, 11.88) * mm});
            skLineSegment(sketch, "E122.5.0.9", {"start": v(542.25, 39) * mm, "end": v(542.25, 16.44) * mm});
            skLineSegment(sketch, "E122.5.0.10", {"start": v(516.44, 42.25) * mm, "end": v(539, 42.25) * mm});
            skArc(sketch, "E122.5.0.11", {"start": v(542.25, 39) * mm, "mid": v(541.3, 41.3) * mm, "end": v(539, 42.25) * mm});
            skLineSegment(sketch, "E122.5.0.12", {"start": v(457.75, -10.99) * mm, "end": v(457.75, 10.99) * mm});
            skLineSegment(sketch, "E122.5.0.13", {"start": v(489.01, 42.25) * mm, "end": v(510.99, 42.25) * mm});
            skLineSegment(sketch, "E122.5.0.14", {"start": v(542.25, -16.44) * mm, "end": v(542.25, -39) * mm});
            skLineSegment(sketch, "E122.5.0.15", {"start": v(539, -42.25) * mm, "end": v(516.44, -42.25) * mm});
            skLineSegment(sketch, "E122.5.0.16", {"start": v(545, -11.88) * mm, "end": v(545, -39) * mm});
            skArc(sketch, "E122.5.0.17", {"start": v(539, -42.25) * mm, "mid": v(541.3, -41.3) * mm, "end": v(542.25, -39) * mm});
            skArc(sketch, "E122.5.0.18", {"start": v(539, -45) * mm, "mid": v(543.24, -43.24) * mm, "end": v(545, -39) * mm});
            skArc(sketch, "E122.5.0.19", {"start": v(479.47, 23) * mm, "mid": v(480.7, 23.41) * mm, "end": v(481.4, 24.48) * mm});
            skLineSegment(sketch, "E122.5.0.20", {"start": v(460.27, -14.5) * mm, "end": v(475.52, -18.6) * mm});
            skArc(sketch, "E122.5.0.21", {"start": v(461, 42.25) * mm, "mid": v(458.7, 41.3) * mm, "end": v(457.75, 39) * mm});
            skLineSegment(sketch, "E122.5.0.22", {"start": v(457.75, 10.99) * mm, "end": v(475.74, 15.8) * mm});
            skLineSegment(sketch, "E122.5.0.23", {"start": v(457.75, 16.44) * mm, "end": v(457.75, 39) * mm});
            skArc(sketch, "E122.5.0.24", {"start": v(460.27, -14.5) * mm, "mid": v(458.53, -14.85) * mm, "end": v(457.75, -16.44) * mm});
            skLineSegment(sketch, "E122.5.0.25", {"start": v(461, 42.25) * mm, "end": v(483.56, 42.25) * mm});
            skArc(sketch, "E122.5.0.26", {"start": v(480.75, 20.25) * mm, "mid": v(480.04, 19.96) * mm, "end": v(479.75, 19.25) * mm});
            skArc(sketch, "E122.5.0.27", {"start": v(461, 45) * mm, "mid": v(456.76, 43.24) * mm, "end": v(455, 39) * mm});
            skLineSegment(sketch, "E122.5.0.28", {"start": v(475.52, 18.6) * mm, "end": v(460.27, 14.5) * mm});
            skLineSegment(sketch, "E122.5.0.29", {"start": v(475.74, -15.8) * mm, "end": v(457.75, -10.99) * mm});
            skArc(sketch, "E122.5.0.30", {"start": v(457.75, 16.44) * mm, "mid": v(458.53, 14.85) * mm, "end": v(460.27, 14.5) * mm});
            skLineSegment(sketch, "E122.5.0.31", {"start": v(485.5, 39.73) * mm, "end": v(481.4, 24.48) * mm});
            skArc(sketch, "E122.5.0.32", {"start": v(481.4, -24.48) * mm, "mid": v(480.7, -23.41) * mm, "end": v(479.47, -23) * mm});
            skLineSegment(sketch, "E122.5.0.33", {"start": v(477, -9.27) * mm, "end": v(477, -14.84) * mm});
            skArc(sketch, "E122.5.0.34", {"start": v(479.7, 7.07) * mm, "mid": v(479.74, 7.23) * mm, "end": v(479.75, 7.4) * mm});
            skLineSegment(sketch, "E122.5.0.35", {"start": v(477, 21) * mm, "end": v(477, 20.53) * mm});
            skArc(sketch, "E122.5.0.36", {"start": v(509.27, -23) * mm, "mid": v(509.06, -23.02) * mm, "end": v(508.86, -23.09) * mm});
            skArc(sketch, "E122.5.0.37", {"start": v(492.93, -20.3) * mm, "mid": v(500, -21.5) * mm, "end": v(507.07, -20.3) * mm});
            skLineSegment(sketch, "E122.5.0.38", {"start": v(480.75, 20.25) * mm, "end": v(492.6, 20.25) * mm});
            skLineSegment(sketch, "E122.5.0.39", {"start": v(514.5, -39.73) * mm, "end": v(518.6, -24.48) * mm});
            skLineSegment(sketch, "E122.5.0.40", {"start": v(510.99, -42.25) * mm, "end": v(489.01, -42.25) * mm});
            skArc(sketch, "E122.5.0.41", {"start": v(479.75, -7.4) * mm, "mid": v(479.74, -7.23) * mm, "end": v(479.7, -7.07) * mm});
            skLineSegment(sketch, "E122.5.0.42", {"start": v(481.4, -24.48) * mm, "end": v(485.5, -39.73) * mm});
            skLineSegment(sketch, "E122.5.0.43", {"start": v(479.75, -19.25) * mm, "end": v(479.75, -7.4) * mm});
            skArc(sketch, "E122.5.0.44", {"start": v(492.93, -20.3) * mm, "mid": v(492.77, -20.26) * mm, "end": v(492.6, -20.25) * mm});
            skArc(sketch, "E122.5.0.45", {"start": v(476.91, 8.86) * mm, "mid": v(475, 0) * mm, "end": v(476.91, -8.86) * mm});
            skLineSegment(sketch, "E122.5.0.46", {"start": v(485.16, -23) * mm, "end": v(490.73, -23) * mm});
            skArc(sketch, "E122.5.0.47", {"start": v(520.53, -23) * mm, "mid": v(519.3, -23.41) * mm, "end": v(518.6, -24.48) * mm});
            skArc(sketch, "E122.5.0.48", {"start": v(485.16, -23) * mm, "mid": v(484.36, -23.4) * mm, "end": v(484.2, -24.26) * mm});
            skLineSegment(sketch, "E122.5.0.49", {"start": v(515.8, -24.26) * mm, "end": v(510.99, -42.25) * mm});
            skArc(sketch, "E122.5.0.50", {"start": v(475.52, 18.6) * mm, "mid": v(476.59, 19.3) * mm, "end": v(477, 20.53) * mm});
            skArc(sketch, "E122.5.0.51", {"start": v(483.56, -42.25) * mm, "mid": v(485.15, -41.47) * mm, "end": v(485.5, -39.73) * mm});
            skArc(sketch, "E122.5.0.52", {"start": v(477, -9.27) * mm, "mid": v(476.98, -9.06) * mm, "end": v(476.91, -8.86) * mm});
            skArc(sketch, "E122.5.0.53", {"start": v(507.4, -20.25) * mm, "mid": v(507.23, -20.26) * mm, "end": v(507.07, -20.3) * mm});
            skArc(sketch, "E122.5.0.54", {"start": v(479.7, 7.07) * mm, "mid": v(478.5, 0) * mm, "end": v(479.7, -7.07) * mm});
            skLineSegment(sketch, "E122.5.0.55", {"start": v(490.73, 23) * mm, "end": v(485.16, 23) * mm});
            skArc(sketch, "E122.5.0.56", {"start": v(491.14, -23.09) * mm, "mid": v(500, -25) * mm, "end": v(508.86, -23.09) * mm});
            skLineSegment(sketch, "E122.5.0.57", {"start": v(492.6, -20.25) * mm, "end": v(480.75, -20.25) * mm});
            skLineSegment(sketch, "E122.5.0.58", {"start": v(479.75, 7.4) * mm, "end": v(479.75, 19.25) * mm});
            skLineSegment(sketch, "E122.5.0.59", {"start": v(519.25, -20.25) * mm, "end": v(507.4, -20.25) * mm});
            skLineSegment(sketch, "E122.5.0.60", {"start": v(489.01, -42.25) * mm, "end": v(484.2, -24.26) * mm});
            skLineSegment(sketch, "E122.5.0.61", {"start": v(477, -20.53) * mm, "end": v(477, -21) * mm});
            skArc(sketch, "E122.5.0.62", {"start": v(514.5, -39.73) * mm, "mid": v(514.85, -41.47) * mm, "end": v(516.44, -42.25) * mm});
            skArc(sketch, "E122.5.0.63", {"start": v(491.14, -23.09) * mm, "mid": v(490.94, -23.02) * mm, "end": v(490.73, -23) * mm});
            skArc(sketch, "E122.5.0.64", {"start": v(508.86, 23.09) * mm, "mid": v(500, 25) * mm, "end": v(491.14, 23.09) * mm});
            skLineSegment(sketch, "E122.5.0.65", {"start": v(509.27, -23) * mm, "end": v(514.84, -23) * mm});
            skLineSegment(sketch, "E122.5.0.66", {"start": v(477, 14.84) * mm, "end": v(477, 9.27) * mm});
            skLineSegment(sketch, "E122.5.0.67", {"start": v(479.47, 23) * mm, "end": v(479, 23) * mm});
            skArc(sketch, "E122.5.0.68", {"start": v(515.8, -24.26) * mm, "mid": v(515.64, -23.4) * mm, "end": v(514.84, -23) * mm});
            skLineSegment(sketch, "E122.5.0.69", {"start": v(484.2, 24.26) * mm, "end": v(489.01, 42.25) * mm});
            skArc(sketch, "E122.5.0.70", {"start": v(475.74, -15.8) * mm, "mid": v(476.6, -15.64) * mm, "end": v(477, -14.84) * mm});
            skLineSegment(sketch, "E122.5.0.71", {"start": v(479, -23) * mm, "end": v(479.47, -23) * mm});
            skArc(sketch, "E122.5.0.72", {"start": v(477, 14.84) * mm, "mid": v(476.6, 15.64) * mm, "end": v(475.74, 15.8) * mm});
            skArc(sketch, "E122.5.0.73", {"start": v(484.2, 24.26) * mm, "mid": v(484.36, 23.4) * mm, "end": v(485.16, 23) * mm});
            skArc(sketch, "E122.5.0.74", {"start": v(507.07, 20.3) * mm, "mid": v(500, 21.5) * mm, "end": v(492.93, 20.3) * mm});
            skArc(sketch, "E122.5.0.75", {"start": v(477, -21) * mm, "mid": v(477.59, -22.41) * mm, "end": v(479, -23) * mm});
            skArc(sketch, "E122.5.0.76", {"start": v(492.6, 20.25) * mm, "mid": v(492.77, 20.26) * mm, "end": v(492.93, 20.3) * mm});
            skArc(sketch, "E122.5.0.77", {"start": v(479, 23) * mm, "mid": v(477.59, 22.41) * mm, "end": v(477, 21) * mm});
            skArc(sketch, "E122.5.0.78", {"start": v(479.75, -19.25) * mm, "mid": v(480.04, -19.96) * mm, "end": v(480.75, -20.25) * mm});
            skArc(sketch, "E122.5.0.79", {"start": v(490.73, 23) * mm, "mid": v(490.94, 23.02) * mm, "end": v(491.14, 23.09) * mm});
            skArc(sketch, "E122.5.0.80", {"start": v(476.91, 8.86) * mm, "mid": v(476.98, 9.06) * mm, "end": v(477, 9.27) * mm});
            skArc(sketch, "E122.5.0.81", {"start": v(477, -20.53) * mm, "mid": v(476.59, -19.3) * mm, "end": v(475.52, -18.6) * mm});
            skLineSegment(sketch, "E122.5.0.82", {"start": v(539.73, 14.5) * mm, "end": v(524.48, 18.6) * mm});
            skLineSegment(sketch, "E122.5.0.83", {"start": v(518.6, 24.48) * mm, "end": v(514.5, 39.73) * mm});
            skArc(sketch, "E122.5.0.84", {"start": v(524.26, 15.8) * mm, "mid": v(523.4, 15.64) * mm, "end": v(523, 14.84) * mm});
            skArc(sketch, "E122.5.0.85", {"start": v(519.25, -20.25) * mm, "mid": v(519.96, -19.96) * mm, "end": v(520.25, -19.25) * mm});
            skLineSegment(sketch, "E122.5.0.86", {"start": v(543.43, 10.67) * mm, "end": v(524.26, 15.8) * mm});
            skArc(sketch, "E122.5.0.87", {"start": v(485.5, 39.73) * mm, "mid": v(485.15, 41.47) * mm, "end": v(483.56, 42.25) * mm});
            skArc(sketch, "E122.5.0.88", {"start": v(523, 21) * mm, "mid": v(522.41, 22.41) * mm, "end": v(521, 23) * mm});
            skArc(sketch, "E122.5.0.89", {"start": v(539.73, 14.5) * mm, "mid": v(541.47, 14.85) * mm, "end": v(542.25, 16.44) * mm});
            skArc(sketch, "E122.5.0.90", {"start": v(523.09, -8.86) * mm, "mid": v(525, 0) * mm, "end": v(523.09, 8.86) * mm});
            skArc(sketch, "E122.5.0.91", {"start": v(520.3, -7.07) * mm, "mid": v(521.5, 0) * mm, "end": v(520.3, 7.07) * mm});
            skLineSegment(sketch, "E122.5.0.92", {"start": v(514.84, 23) * mm, "end": v(509.27, 23) * mm});
            skArc(sketch, "E122.5.0.93", {"start": v(523, 9.27) * mm, "mid": v(523.02, 9.06) * mm, "end": v(523.09, 8.86) * mm});
            skLineSegment(sketch, "E122.5.0.94", {"start": v(524.26, -15.8) * mm, "end": v(543.43, -10.67) * mm});
            skArc(sketch, "E122.5.0.95", {"start": v(542.25, -16.44) * mm, "mid": v(541.47, -14.85) * mm, "end": v(539.73, -14.5) * mm});
            skArc(sketch, "E122.5.0.96", {"start": v(523.09, -8.86) * mm, "mid": v(523.02, -9.06) * mm, "end": v(523, -9.27) * mm});
            skArc(sketch, "E122.5.0.97", {"start": v(523, -14.84) * mm, "mid": v(523.4, -15.64) * mm, "end": v(524.26, -15.8) * mm});
            skArc(sketch, "E122.5.0.98", {"start": v(516.44, 42.25) * mm, "mid": v(514.85, 41.47) * mm, "end": v(514.5, 39.73) * mm});
            skArc(sketch, "E122.5.0.99", {"start": v(545, -11.88) * mm, "mid": v(544.51, -10.89) * mm, "end": v(543.43, -10.67) * mm});
            skLineSegment(sketch, "E122.5.0.100", {"start": v(523, 20.53) * mm, "end": v(523, 21) * mm});
            skLineSegment(sketch, "E122.5.0.101", {"start": v(523, -9.27) * mm, "end": v(523, -14.84) * mm});
            skLineSegment(sketch, "E122.5.0.102", {"start": v(520.25, 19.25) * mm, "end": v(520.25, 7.4) * mm});
            skLineSegment(sketch, "E122.5.0.103", {"start": v(520.25, -7.4) * mm, "end": v(520.25, -19.25) * mm});
            skLineSegment(sketch, "E122.5.0.104", {"start": v(510.99, 42.25) * mm, "end": v(515.8, 24.26) * mm});
            skLineSegment(sketch, "E122.5.0.105", {"start": v(507.4, 20.25) * mm, "end": v(519.25, 20.25) * mm});
            skArc(sketch, "E122.5.0.106", {"start": v(543.43, 10.67) * mm, "mid": v(544.51, 10.89) * mm, "end": v(545, 11.88) * mm});
            skArc(sketch, "E122.5.0.107", {"start": v(514.84, 23) * mm, "mid": v(515.64, 23.4) * mm, "end": v(515.8, 24.26) * mm});
            skLineSegment(sketch, "E122.5.0.108", {"start": v(524.48, -18.6) * mm, "end": v(539.73, -14.5) * mm});
            skLineSegment(sketch, "E122.5.0.109", {"start": v(523, 14.84) * mm, "end": v(523, 9.27) * mm});
            skArc(sketch, "E122.5.0.110", {"start": v(518.6, 24.48) * mm, "mid": v(519.3, 23.41) * mm, "end": v(520.53, 23) * mm});
            skArc(sketch, "E122.5.0.111", {"start": v(520.25, 19.25) * mm, "mid": v(519.96, 19.96) * mm, "end": v(519.25, 20.25) * mm});
            skArc(sketch, "E122.5.0.112", {"start": v(508.86, 23.09) * mm, "mid": v(509.06, 23.02) * mm, "end": v(509.27, 23) * mm});
            skArc(sketch, "E122.5.0.113", {"start": v(520.3, -7.07) * mm, "mid": v(520.26, -7.23) * mm, "end": v(520.25, -7.4) * mm});
            skArc(sketch, "E122.5.0.114", {"start": v(521, -23) * mm, "mid": v(522.41, -22.41) * mm, "end": v(523, -21) * mm});
            skArc(sketch, "E122.5.0.115", {"start": v(507.07, 20.3) * mm, "mid": v(507.23, 20.26) * mm, "end": v(507.4, 20.25) * mm});
            skArc(sketch, "E122.5.0.116", {"start": v(520.25, 7.4) * mm, "mid": v(520.26, 7.23) * mm, "end": v(520.3, 7.07) * mm});
            skArc(sketch, "E122.5.0.117", {"start": v(523, 20.53) * mm, "mid": v(523.41, 19.3) * mm, "end": v(524.48, 18.6) * mm});
            skLineSegment(sketch, "E122.5.0.118", {"start": v(523, -21) * mm, "end": v(523, -20.53) * mm});
            skLineSegment(sketch, "E122.5.0.119", {"start": v(521, 23) * mm, "end": v(520.53, 23) * mm});
            skLineSegment(sketch, "E122.5.0.120", {"start": v(520.53, -23) * mm, "end": v(521, -23) * mm});
            skArc(sketch, "E122.5.0.121", {"start": v(524.48, -18.6) * mm, "mid": v(523.41, -19.3) * mm, "end": v(523, -20.53) * mm});
            skArc(sketch, "E122.6.0.0", {"start": v(555, -39) * mm, "mid": v(556.76, -43.24) * mm, "end": v(561, -45) * mm});
            skLineSegment(sketch, "E122.6.0.1", {"start": v(555, -39) * mm, "end": v(555, 39) * mm});
            skArc(sketch, "E122.6.0.2", {"start": v(557.75, -39) * mm, "mid": v(558.7, -41.3) * mm, "end": v(561, -42.25) * mm});
            skLineSegment(sketch, "E122.6.0.3", {"start": v(639, -45) * mm, "end": v(561, -45) * mm});
            skLineSegment(sketch, "E122.6.0.4", {"start": v(557.75, -39) * mm, "end": v(557.75, -16.44) * mm});
            skLineSegment(sketch, "E122.6.0.5", {"start": v(583.56, -42.25) * mm, "end": v(561, -42.25) * mm});
            skLineSegment(sketch, "E122.6.0.6", {"start": v(561, 45) * mm, "end": v(639, 45) * mm});
            skArc(sketch, "E122.6.0.7", {"start": v(645, 39) * mm, "mid": v(643.24, 43.24) * mm, "end": v(639, 45) * mm});
            skLineSegment(sketch, "E122.6.0.8", {"start": v(645, 39) * mm, "end": v(645, 11.88) * mm});
            skLineSegment(sketch, "E122.6.0.9", {"start": v(642.25, 39) * mm, "end": v(642.25, 16.44) * mm});
            skLineSegment(sketch, "E122.6.0.10", {"start": v(616.44, 42.25) * mm, "end": v(639, 42.25) * mm});
            skArc(sketch, "E122.6.0.11", {"start": v(642.25, 39) * mm, "mid": v(641.3, 41.3) * mm, "end": v(639, 42.25) * mm});
            skLineSegment(sketch, "E122.6.0.12", {"start": v(557.75, -10.99) * mm, "end": v(557.75, 10.99) * mm});
            skLineSegment(sketch, "E122.6.0.13", {"start": v(589.01, 42.25) * mm, "end": v(610.99, 42.25) * mm});
            skLineSegment(sketch, "E122.6.0.14", {"start": v(642.25, -16.44) * mm, "end": v(642.25, -39) * mm});
            skLineSegment(sketch, "E122.6.0.15", {"start": v(639, -42.25) * mm, "end": v(616.44, -42.25) * mm});
            skLineSegment(sketch, "E122.6.0.16", {"start": v(645, -11.88) * mm, "end": v(645, -39) * mm});
            skArc(sketch, "E122.6.0.17", {"start": v(639, -42.25) * mm, "mid": v(641.3, -41.3) * mm, "end": v(642.25, -39) * mm});
            skArc(sketch, "E122.6.0.18", {"start": v(639, -45) * mm, "mid": v(643.24, -43.24) * mm, "end": v(645, -39) * mm});
            skArc(sketch, "E122.6.0.19", {"start": v(579.47, 23) * mm, "mid": v(580.7, 23.41) * mm, "end": v(581.4, 24.48) * mm});
            skLineSegment(sketch, "E122.6.0.20", {"start": v(560.27, -14.5) * mm, "end": v(575.52, -18.6) * mm});
            skArc(sketch, "E122.6.0.21", {"start": v(561, 42.25) * mm, "mid": v(558.7, 41.3) * mm, "end": v(557.75, 39) * mm});
            skLineSegment(sketch, "E122.6.0.22", {"start": v(557.75, 10.99) * mm, "end": v(575.74, 15.8) * mm});
            skLineSegment(sketch, "E122.6.0.23", {"start": v(557.75, 16.44) * mm, "end": v(557.75, 39) * mm});
            skArc(sketch, "E122.6.0.24", {"start": v(560.27, -14.5) * mm, "mid": v(558.53, -14.85) * mm, "end": v(557.75, -16.44) * mm});
            skLineSegment(sketch, "E122.6.0.25", {"start": v(561, 42.25) * mm, "end": v(583.56, 42.25) * mm});
            skArc(sketch, "E122.6.0.26", {"start": v(580.75, 20.25) * mm, "mid": v(580.04, 19.96) * mm, "end": v(579.75, 19.25) * mm});
            skArc(sketch, "E122.6.0.27", {"start": v(561, 45) * mm, "mid": v(556.76, 43.24) * mm, "end": v(555, 39) * mm});
            skLineSegment(sketch, "E122.6.0.28", {"start": v(575.52, 18.6) * mm, "end": v(560.27, 14.5) * mm});
            skLineSegment(sketch, "E122.6.0.29", {"start": v(575.74, -15.8) * mm, "end": v(557.75, -10.99) * mm});
            skArc(sketch, "E122.6.0.30", {"start": v(557.75, 16.44) * mm, "mid": v(558.53, 14.85) * mm, "end": v(560.27, 14.5) * mm});
            skLineSegment(sketch, "E122.6.0.31", {"start": v(585.5, 39.73) * mm, "end": v(581.4, 24.48) * mm});
            skArc(sketch, "E122.6.0.32", {"start": v(581.4, -24.48) * mm, "mid": v(580.7, -23.41) * mm, "end": v(579.47, -23) * mm});
            skLineSegment(sketch, "E122.6.0.33", {"start": v(577, -9.27) * mm, "end": v(577, -14.84) * mm});
            skArc(sketch, "E122.6.0.34", {"start": v(579.7, 7.07) * mm, "mid": v(579.74, 7.23) * mm, "end": v(579.75, 7.4) * mm});
            skLineSegment(sketch, "E122.6.0.35", {"start": v(577, 21) * mm, "end": v(577, 20.53) * mm});
            skArc(sketch, "E122.6.0.36", {"start": v(609.27, -23) * mm, "mid": v(609.06, -23.02) * mm, "end": v(608.86, -23.09) * mm});
            skArc(sketch, "E122.6.0.37", {"start": v(592.93, -20.3) * mm, "mid": v(600, -21.5) * mm, "end": v(607.07, -20.3) * mm});
            skLineSegment(sketch, "E122.6.0.38", {"start": v(580.75, 20.25) * mm, "end": v(592.6, 20.25) * mm});
            skLineSegment(sketch, "E122.6.0.39", {"start": v(614.5, -39.73) * mm, "end": v(618.6, -24.48) * mm});
            skLineSegment(sketch, "E122.6.0.40", {"start": v(610.99, -42.25) * mm, "end": v(589.01, -42.25) * mm});
            skArc(sketch, "E122.6.0.41", {"start": v(579.75, -7.4) * mm, "mid": v(579.74, -7.23) * mm, "end": v(579.7, -7.07) * mm});
            skLineSegment(sketch, "E122.6.0.42", {"start": v(581.4, -24.48) * mm, "end": v(585.5, -39.73) * mm});
            skLineSegment(sketch, "E122.6.0.43", {"start": v(579.75, -19.25) * mm, "end": v(579.75, -7.4) * mm});
            skArc(sketch, "E122.6.0.44", {"start": v(592.93, -20.3) * mm, "mid": v(592.77, -20.26) * mm, "end": v(592.6, -20.25) * mm});
            skArc(sketch, "E122.6.0.45", {"start": v(576.91, 8.86) * mm, "mid": v(575, 0) * mm, "end": v(576.91, -8.86) * mm});
            skLineSegment(sketch, "E122.6.0.46", {"start": v(585.16, -23) * mm, "end": v(590.73, -23) * mm});
            skArc(sketch, "E122.6.0.47", {"start": v(620.53, -23) * mm, "mid": v(619.3, -23.41) * mm, "end": v(618.6, -24.48) * mm});
            skArc(sketch, "E122.6.0.48", {"start": v(585.16, -23) * mm, "mid": v(584.36, -23.4) * mm, "end": v(584.2, -24.26) * mm});
            skLineSegment(sketch, "E122.6.0.49", {"start": v(615.8, -24.26) * mm, "end": v(610.99, -42.25) * mm});
            skArc(sketch, "E122.6.0.50", {"start": v(575.52, 18.6) * mm, "mid": v(576.59, 19.3) * mm, "end": v(577, 20.53) * mm});
            skArc(sketch, "E122.6.0.51", {"start": v(583.56, -42.25) * mm, "mid": v(585.15, -41.47) * mm, "end": v(585.5, -39.73) * mm});
            skArc(sketch, "E122.6.0.52", {"start": v(577, -9.27) * mm, "mid": v(576.98, -9.06) * mm, "end": v(576.91, -8.86) * mm});
            skArc(sketch, "E122.6.0.53", {"start": v(607.4, -20.25) * mm, "mid": v(607.23, -20.26) * mm, "end": v(607.07, -20.3) * mm});
            skArc(sketch, "E122.6.0.54", {"start": v(579.7, 7.07) * mm, "mid": v(578.5, 0) * mm, "end": v(579.7, -7.07) * mm});
            skLineSegment(sketch, "E122.6.0.55", {"start": v(590.73, 23) * mm, "end": v(585.16, 23) * mm});
            skArc(sketch, "E122.6.0.56", {"start": v(591.14, -23.09) * mm, "mid": v(600, -25) * mm, "end": v(608.86, -23.09) * mm});
            skLineSegment(sketch, "E122.6.0.57", {"start": v(592.6, -20.25) * mm, "end": v(580.75, -20.25) * mm});
            skLineSegment(sketch, "E122.6.0.58", {"start": v(579.75, 7.4) * mm, "end": v(579.75, 19.25) * mm});
            skLineSegment(sketch, "E122.6.0.59", {"start": v(619.25, -20.25) * mm, "end": v(607.4, -20.25) * mm});
            skLineSegment(sketch, "E122.6.0.60", {"start": v(589.01, -42.25) * mm, "end": v(584.2, -24.26) * mm});
            skLineSegment(sketch, "E122.6.0.61", {"start": v(577, -20.53) * mm, "end": v(577, -21) * mm});
            skArc(sketch, "E122.6.0.62", {"start": v(614.5, -39.73) * mm, "mid": v(614.85, -41.47) * mm, "end": v(616.44, -42.25) * mm});
            skArc(sketch, "E122.6.0.63", {"start": v(591.14, -23.09) * mm, "mid": v(590.94, -23.02) * mm, "end": v(590.73, -23) * mm});
            skArc(sketch, "E122.6.0.64", {"start": v(608.86, 23.09) * mm, "mid": v(600, 25) * mm, "end": v(591.14, 23.09) * mm});
            skLineSegment(sketch, "E122.6.0.65", {"start": v(609.27, -23) * mm, "end": v(614.84, -23) * mm});
            skLineSegment(sketch, "E122.6.0.66", {"start": v(577, 14.84) * mm, "end": v(577, 9.27) * mm});
            skLineSegment(sketch, "E122.6.0.67", {"start": v(579.47, 23) * mm, "end": v(579, 23) * mm});
            skArc(sketch, "E122.6.0.68", {"start": v(615.8, -24.26) * mm, "mid": v(615.64, -23.4) * mm, "end": v(614.84, -23) * mm});
            skLineSegment(sketch, "E122.6.0.69", {"start": v(584.2, 24.26) * mm, "end": v(589.01, 42.25) * mm});
            skArc(sketch, "E122.6.0.70", {"start": v(575.74, -15.8) * mm, "mid": v(576.6, -15.64) * mm, "end": v(577, -14.84) * mm});
            skLineSegment(sketch, "E122.6.0.71", {"start": v(579, -23) * mm, "end": v(579.47, -23) * mm});
            skArc(sketch, "E122.6.0.72", {"start": v(577, 14.84) * mm, "mid": v(576.6, 15.64) * mm, "end": v(575.74, 15.8) * mm});
            skArc(sketch, "E122.6.0.73", {"start": v(584.2, 24.26) * mm, "mid": v(584.36, 23.4) * mm, "end": v(585.16, 23) * mm});
            skArc(sketch, "E122.6.0.74", {"start": v(607.07, 20.3) * mm, "mid": v(600, 21.5) * mm, "end": v(592.93, 20.3) * mm});
            skArc(sketch, "E122.6.0.75", {"start": v(577, -21) * mm, "mid": v(577.59, -22.41) * mm, "end": v(579, -23) * mm});
            skArc(sketch, "E122.6.0.76", {"start": v(592.6, 20.25) * mm, "mid": v(592.77, 20.26) * mm, "end": v(592.93, 20.3) * mm});
            skArc(sketch, "E122.6.0.77", {"start": v(579, 23) * mm, "mid": v(577.59, 22.41) * mm, "end": v(577, 21) * mm});
            skArc(sketch, "E122.6.0.78", {"start": v(579.75, -19.25) * mm, "mid": v(580.04, -19.96) * mm, "end": v(580.75, -20.25) * mm});
            skArc(sketch, "E122.6.0.79", {"start": v(590.73, 23) * mm, "mid": v(590.94, 23.02) * mm, "end": v(591.14, 23.09) * mm});
            skArc(sketch, "E122.6.0.80", {"start": v(576.91, 8.86) * mm, "mid": v(576.98, 9.06) * mm, "end": v(577, 9.27) * mm});
            skArc(sketch, "E122.6.0.81", {"start": v(577, -20.53) * mm, "mid": v(576.59, -19.3) * mm, "end": v(575.52, -18.6) * mm});
            skLineSegment(sketch, "E122.6.0.82", {"start": v(639.73, 14.5) * mm, "end": v(624.48, 18.6) * mm});
            skLineSegment(sketch, "E122.6.0.83", {"start": v(618.6, 24.48) * mm, "end": v(614.5, 39.73) * mm});
            skArc(sketch, "E122.6.0.84", {"start": v(624.26, 15.8) * mm, "mid": v(623.4, 15.64) * mm, "end": v(623, 14.84) * mm});
            skArc(sketch, "E122.6.0.85", {"start": v(619.25, -20.25) * mm, "mid": v(619.96, -19.96) * mm, "end": v(620.25, -19.25) * mm});
            skLineSegment(sketch, "E122.6.0.86", {"start": v(643.43, 10.67) * mm, "end": v(624.26, 15.8) * mm});
            skArc(sketch, "E122.6.0.87", {"start": v(585.5, 39.73) * mm, "mid": v(585.15, 41.47) * mm, "end": v(583.56, 42.25) * mm});
            skArc(sketch, "E122.6.0.88", {"start": v(623, 21) * mm, "mid": v(622.41, 22.41) * mm, "end": v(621, 23) * mm});
            skArc(sketch, "E122.6.0.89", {"start": v(639.73, 14.5) * mm, "mid": v(641.47, 14.85) * mm, "end": v(642.25, 16.44) * mm});
            skArc(sketch, "E122.6.0.90", {"start": v(623.09, -8.86) * mm, "mid": v(625, 0) * mm, "end": v(623.09, 8.86) * mm});
            skArc(sketch, "E122.6.0.91", {"start": v(620.3, -7.07) * mm, "mid": v(621.5, 0) * mm, "end": v(620.3, 7.07) * mm});
            skLineSegment(sketch, "E122.6.0.92", {"start": v(614.84, 23) * mm, "end": v(609.27, 23) * mm});
            skArc(sketch, "E122.6.0.93", {"start": v(623, 9.27) * mm, "mid": v(623.02, 9.06) * mm, "end": v(623.09, 8.86) * mm});
            skLineSegment(sketch, "E122.6.0.94", {"start": v(624.26, -15.8) * mm, "end": v(643.43, -10.67) * mm});
            skArc(sketch, "E122.6.0.95", {"start": v(642.25, -16.44) * mm, "mid": v(641.47, -14.85) * mm, "end": v(639.73, -14.5) * mm});
            skArc(sketch, "E122.6.0.96", {"start": v(623.09, -8.86) * mm, "mid": v(623.02, -9.06) * mm, "end": v(623, -9.27) * mm});
            skArc(sketch, "E122.6.0.97", {"start": v(623, -14.84) * mm, "mid": v(623.4, -15.64) * mm, "end": v(624.26, -15.8) * mm});
            skArc(sketch, "E122.6.0.98", {"start": v(616.44, 42.25) * mm, "mid": v(614.85, 41.47) * mm, "end": v(614.5, 39.73) * mm});
            skArc(sketch, "E122.6.0.99", {"start": v(645, -11.88) * mm, "mid": v(644.51, -10.89) * mm, "end": v(643.43, -10.67) * mm});
            skLineSegment(sketch, "E122.6.0.100", {"start": v(623, 20.53) * mm, "end": v(623, 21) * mm});
            skLineSegment(sketch, "E122.6.0.101", {"start": v(623, -9.27) * mm, "end": v(623, -14.84) * mm});
            skLineSegment(sketch, "E122.6.0.102", {"start": v(620.25, 19.25) * mm, "end": v(620.25, 7.4) * mm});
            skLineSegment(sketch, "E122.6.0.103", {"start": v(620.25, -7.4) * mm, "end": v(620.25, -19.25) * mm});
            skLineSegment(sketch, "E122.6.0.104", {"start": v(610.99, 42.25) * mm, "end": v(615.8, 24.26) * mm});
            skLineSegment(sketch, "E122.6.0.105", {"start": v(607.4, 20.25) * mm, "end": v(619.25, 20.25) * mm});
            skArc(sketch, "E122.6.0.106", {"start": v(643.43, 10.67) * mm, "mid": v(644.51, 10.89) * mm, "end": v(645, 11.88) * mm});
            skArc(sketch, "E122.6.0.107", {"start": v(614.84, 23) * mm, "mid": v(615.64, 23.4) * mm, "end": v(615.8, 24.26) * mm});
            skLineSegment(sketch, "E122.6.0.108", {"start": v(624.48, -18.6) * mm, "end": v(639.73, -14.5) * mm});
            skLineSegment(sketch, "E122.6.0.109", {"start": v(623, 14.84) * mm, "end": v(623, 9.27) * mm});
            skArc(sketch, "E122.6.0.110", {"start": v(618.6, 24.48) * mm, "mid": v(619.3, 23.41) * mm, "end": v(620.53, 23) * mm});
            skArc(sketch, "E122.6.0.111", {"start": v(620.25, 19.25) * mm, "mid": v(619.96, 19.96) * mm, "end": v(619.25, 20.25) * mm});
            skArc(sketch, "E122.6.0.112", {"start": v(608.86, 23.09) * mm, "mid": v(609.06, 23.02) * mm, "end": v(609.27, 23) * mm});
            skArc(sketch, "E122.6.0.113", {"start": v(620.3, -7.07) * mm, "mid": v(620.26, -7.23) * mm, "end": v(620.25, -7.4) * mm});
            skArc(sketch, "E122.6.0.114", {"start": v(621, -23) * mm, "mid": v(622.41, -22.41) * mm, "end": v(623, -21) * mm});
            skArc(sketch, "E122.6.0.115", {"start": v(607.07, 20.3) * mm, "mid": v(607.23, 20.26) * mm, "end": v(607.4, 20.25) * mm});
            skArc(sketch, "E122.6.0.116", {"start": v(620.25, 7.4) * mm, "mid": v(620.26, 7.23) * mm, "end": v(620.3, 7.07) * mm});
            skArc(sketch, "E122.6.0.117", {"start": v(623, 20.53) * mm, "mid": v(623.41, 19.3) * mm, "end": v(624.48, 18.6) * mm});
            skLineSegment(sketch, "E122.6.0.118", {"start": v(623, -21) * mm, "end": v(623, -20.53) * mm});
            skLineSegment(sketch, "E122.6.0.119", {"start": v(621, 23) * mm, "end": v(620.53, 23) * mm});
            skLineSegment(sketch, "E122.6.0.120", {"start": v(620.53, -23) * mm, "end": v(621, -23) * mm});
            skArc(sketch, "E122.6.0.121", {"start": v(624.48, -18.6) * mm, "mid": v(623.41, -19.3) * mm, "end": v(623, -20.53) * mm});
            skArc(sketch, "E122.7.0.0", {"start": v(655, -39) * mm, "mid": v(656.76, -43.24) * mm, "end": v(661, -45) * mm});
            skLineSegment(sketch, "E122.7.0.1", {"start": v(655, -39) * mm, "end": v(655, 39) * mm});
            skArc(sketch, "E122.7.0.2", {"start": v(657.75, -39) * mm, "mid": v(658.7, -41.3) * mm, "end": v(661, -42.25) * mm});
            skLineSegment(sketch, "E122.7.0.3", {"start": v(739, -45) * mm, "end": v(661, -45) * mm});
            skLineSegment(sketch, "E122.7.0.4", {"start": v(657.75, -39) * mm, "end": v(657.75, -16.44) * mm});
            skLineSegment(sketch, "E122.7.0.5", {"start": v(683.56, -42.25) * mm, "end": v(661, -42.25) * mm});
            skLineSegment(sketch, "E122.7.0.6", {"start": v(661, 45) * mm, "end": v(739, 45) * mm});
            skArc(sketch, "E122.7.0.7", {"start": v(745, 39) * mm, "mid": v(743.24, 43.24) * mm, "end": v(739, 45) * mm});
            skLineSegment(sketch, "E122.7.0.8", {"start": v(745, 39) * mm, "end": v(745, 11.88) * mm});
            skLineSegment(sketch, "E122.7.0.9", {"start": v(742.25, 39) * mm, "end": v(742.25, 16.44) * mm});
            skLineSegment(sketch, "E122.7.0.10", {"start": v(716.44, 42.25) * mm, "end": v(739, 42.25) * mm});
            skArc(sketch, "E122.7.0.11", {"start": v(742.25, 39) * mm, "mid": v(741.3, 41.3) * mm, "end": v(739, 42.25) * mm});
            skLineSegment(sketch, "E122.7.0.12", {"start": v(657.75, -10.99) * mm, "end": v(657.75, 10.99) * mm});
            skLineSegment(sketch, "E122.7.0.13", {"start": v(689.01, 42.25) * mm, "end": v(710.99, 42.25) * mm});
            skLineSegment(sketch, "E122.7.0.14", {"start": v(742.25, -16.44) * mm, "end": v(742.25, -39) * mm});
            skLineSegment(sketch, "E122.7.0.15", {"start": v(739, -42.25) * mm, "end": v(716.44, -42.25) * mm});
            skLineSegment(sketch, "E122.7.0.16", {"start": v(745, -11.88) * mm, "end": v(745, -39) * mm});
            skArc(sketch, "E122.7.0.17", {"start": v(739, -42.25) * mm, "mid": v(741.3, -41.3) * mm, "end": v(742.25, -39) * mm});
            skArc(sketch, "E122.7.0.18", {"start": v(739, -45) * mm, "mid": v(743.24, -43.24) * mm, "end": v(745, -39) * mm});
            skArc(sketch, "E122.7.0.19", {"start": v(679.47, 23) * mm, "mid": v(680.7, 23.41) * mm, "end": v(681.4, 24.48) * mm});
            skLineSegment(sketch, "E122.7.0.20", {"start": v(660.27, -14.5) * mm, "end": v(675.52, -18.6) * mm});
            skArc(sketch, "E122.7.0.21", {"start": v(661, 42.25) * mm, "mid": v(658.7, 41.3) * mm, "end": v(657.75, 39) * mm});
            skLineSegment(sketch, "E122.7.0.22", {"start": v(657.75, 10.99) * mm, "end": v(675.74, 15.8) * mm});
            skLineSegment(sketch, "E122.7.0.23", {"start": v(657.75, 16.44) * mm, "end": v(657.75, 39) * mm});
            skArc(sketch, "E122.7.0.24", {"start": v(660.27, -14.5) * mm, "mid": v(658.53, -14.85) * mm, "end": v(657.75, -16.44) * mm});
            skLineSegment(sketch, "E122.7.0.25", {"start": v(661, 42.25) * mm, "end": v(683.56, 42.25) * mm});
            skArc(sketch, "E122.7.0.26", {"start": v(680.75, 20.25) * mm, "mid": v(680.04, 19.96) * mm, "end": v(679.75, 19.25) * mm});
            skArc(sketch, "E122.7.0.27", {"start": v(661, 45) * mm, "mid": v(656.76, 43.24) * mm, "end": v(655, 39) * mm});
            skLineSegment(sketch, "E122.7.0.28", {"start": v(675.52, 18.6) * mm, "end": v(660.27, 14.5) * mm});
            skLineSegment(sketch, "E122.7.0.29", {"start": v(675.74, -15.8) * mm, "end": v(657.75, -10.99) * mm});
            skArc(sketch, "E122.7.0.30", {"start": v(657.75, 16.44) * mm, "mid": v(658.53, 14.85) * mm, "end": v(660.27, 14.5) * mm});
            skLineSegment(sketch, "E122.7.0.31", {"start": v(685.5, 39.73) * mm, "end": v(681.4, 24.48) * mm});
            skArc(sketch, "E122.7.0.32", {"start": v(681.4, -24.48) * mm, "mid": v(680.7, -23.41) * mm, "end": v(679.47, -23) * mm});
            skLineSegment(sketch, "E122.7.0.33", {"start": v(677, -9.27) * mm, "end": v(677, -14.84) * mm});
            skArc(sketch, "E122.7.0.34", {"start": v(679.7, 7.07) * mm, "mid": v(679.74, 7.23) * mm, "end": v(679.75, 7.4) * mm});
            skLineSegment(sketch, "E122.7.0.35", {"start": v(677, 21) * mm, "end": v(677, 20.53) * mm});
            skArc(sketch, "E122.7.0.36", {"start": v(709.27, -23) * mm, "mid": v(709.06, -23.02) * mm, "end": v(708.86, -23.09) * mm});
            skArc(sketch, "E122.7.0.37", {"start": v(692.93, -20.3) * mm, "mid": v(700, -21.5) * mm, "end": v(707.07, -20.3) * mm});
            skLineSegment(sketch, "E122.7.0.38", {"start": v(680.75, 20.25) * mm, "end": v(692.6, 20.25) * mm});
            skLineSegment(sketch, "E122.7.0.39", {"start": v(714.5, -39.73) * mm, "end": v(718.6, -24.48) * mm});
            skLineSegment(sketch, "E122.7.0.40", {"start": v(710.99, -42.25) * mm, "end": v(689.01, -42.25) * mm});
            skArc(sketch, "E122.7.0.41", {"start": v(679.75, -7.4) * mm, "mid": v(679.74, -7.23) * mm, "end": v(679.7, -7.07) * mm});
            skLineSegment(sketch, "E122.7.0.42", {"start": v(681.4, -24.48) * mm, "end": v(685.5, -39.73) * mm});
            skLineSegment(sketch, "E122.7.0.43", {"start": v(679.75, -19.25) * mm, "end": v(679.75, -7.4) * mm});
            skArc(sketch, "E122.7.0.44", {"start": v(692.93, -20.3) * mm, "mid": v(692.77, -20.26) * mm, "end": v(692.6, -20.25) * mm});
            skArc(sketch, "E122.7.0.45", {"start": v(676.91, 8.86) * mm, "mid": v(675, 0) * mm, "end": v(676.91, -8.86) * mm});
            skLineSegment(sketch, "E122.7.0.46", {"start": v(685.16, -23) * mm, "end": v(690.73, -23) * mm});
            skArc(sketch, "E122.7.0.47", {"start": v(720.53, -23) * mm, "mid": v(719.3, -23.41) * mm, "end": v(718.6, -24.48) * mm});
            skArc(sketch, "E122.7.0.48", {"start": v(685.16, -23) * mm, "mid": v(684.36, -23.4) * mm, "end": v(684.2, -24.26) * mm});
            skLineSegment(sketch, "E122.7.0.49", {"start": v(715.8, -24.26) * mm, "end": v(710.99, -42.25) * mm});
            skArc(sketch, "E122.7.0.50", {"start": v(675.52, 18.6) * mm, "mid": v(676.59, 19.3) * mm, "end": v(677, 20.53) * mm});
            skArc(sketch, "E122.7.0.51", {"start": v(683.56, -42.25) * mm, "mid": v(685.15, -41.47) * mm, "end": v(685.5, -39.73) * mm});
            skArc(sketch, "E122.7.0.52", {"start": v(677, -9.27) * mm, "mid": v(676.98, -9.06) * mm, "end": v(676.91, -8.86) * mm});
            skArc(sketch, "E122.7.0.53", {"start": v(707.4, -20.25) * mm, "mid": v(707.23, -20.26) * mm, "end": v(707.07, -20.3) * mm});
            skArc(sketch, "E122.7.0.54", {"start": v(679.7, 7.07) * mm, "mid": v(678.5, 0) * mm, "end": v(679.7, -7.07) * mm});
            skLineSegment(sketch, "E122.7.0.55", {"start": v(690.73, 23) * mm, "end": v(685.16, 23) * mm});
            skArc(sketch, "E122.7.0.56", {"start": v(691.14, -23.09) * mm, "mid": v(700, -25) * mm, "end": v(708.86, -23.09) * mm});
            skLineSegment(sketch, "E122.7.0.57", {"start": v(692.6, -20.25) * mm, "end": v(680.75, -20.25) * mm});
            skLineSegment(sketch, "E122.7.0.58", {"start": v(679.75, 7.4) * mm, "end": v(679.75, 19.25) * mm});
            skLineSegment(sketch, "E122.7.0.59", {"start": v(719.25, -20.25) * mm, "end": v(707.4, -20.25) * mm});
            skLineSegment(sketch, "E122.7.0.60", {"start": v(689.01, -42.25) * mm, "end": v(684.2, -24.26) * mm});
            skLineSegment(sketch, "E122.7.0.61", {"start": v(677, -20.53) * mm, "end": v(677, -21) * mm});
            skArc(sketch, "E122.7.0.62", {"start": v(714.5, -39.73) * mm, "mid": v(714.85, -41.47) * mm, "end": v(716.44, -42.25) * mm});
            skArc(sketch, "E122.7.0.63", {"start": v(691.14, -23.09) * mm, "mid": v(690.94, -23.02) * mm, "end": v(690.73, -23) * mm});
            skArc(sketch, "E122.7.0.64", {"start": v(708.86, 23.09) * mm, "mid": v(700, 25) * mm, "end": v(691.14, 23.09) * mm});
            skLineSegment(sketch, "E122.7.0.65", {"start": v(709.27, -23) * mm, "end": v(714.84, -23) * mm});
            skLineSegment(sketch, "E122.7.0.66", {"start": v(677, 14.84) * mm, "end": v(677, 9.27) * mm});
            skLineSegment(sketch, "E122.7.0.67", {"start": v(679.47, 23) * mm, "end": v(679, 23) * mm});
            skArc(sketch, "E122.7.0.68", {"start": v(715.8, -24.26) * mm, "mid": v(715.64, -23.4) * mm, "end": v(714.84, -23) * mm});
            skLineSegment(sketch, "E122.7.0.69", {"start": v(684.2, 24.26) * mm, "end": v(689.01, 42.25) * mm});
            skArc(sketch, "E122.7.0.70", {"start": v(675.74, -15.8) * mm, "mid": v(676.6, -15.64) * mm, "end": v(677, -14.84) * mm});
            skLineSegment(sketch, "E122.7.0.71", {"start": v(679, -23) * mm, "end": v(679.47, -23) * mm});
            skArc(sketch, "E122.7.0.72", {"start": v(677, 14.84) * mm, "mid": v(676.6, 15.64) * mm, "end": v(675.74, 15.8) * mm});
            skArc(sketch, "E122.7.0.73", {"start": v(684.2, 24.26) * mm, "mid": v(684.36, 23.4) * mm, "end": v(685.16, 23) * mm});
            skArc(sketch, "E122.7.0.74", {"start": v(707.07, 20.3) * mm, "mid": v(700, 21.5) * mm, "end": v(692.93, 20.3) * mm});
            skArc(sketch, "E122.7.0.75", {"start": v(677, -21) * mm, "mid": v(677.59, -22.41) * mm, "end": v(679, -23) * mm});
            skArc(sketch, "E122.7.0.76", {"start": v(692.6, 20.25) * mm, "mid": v(692.77, 20.26) * mm, "end": v(692.93, 20.3) * mm});
            skArc(sketch, "E122.7.0.77", {"start": v(679, 23) * mm, "mid": v(677.59, 22.41) * mm, "end": v(677, 21) * mm});
            skArc(sketch, "E122.7.0.78", {"start": v(679.75, -19.25) * mm, "mid": v(680.04, -19.96) * mm, "end": v(680.75, -20.25) * mm});
            skArc(sketch, "E122.7.0.79", {"start": v(690.73, 23) * mm, "mid": v(690.94, 23.02) * mm, "end": v(691.14, 23.09) * mm});
            skArc(sketch, "E122.7.0.80", {"start": v(676.91, 8.86) * mm, "mid": v(676.98, 9.06) * mm, "end": v(677, 9.27) * mm});
            skArc(sketch, "E122.7.0.81", {"start": v(677, -20.53) * mm, "mid": v(676.59, -19.3) * mm, "end": v(675.52, -18.6) * mm});
            skLineSegment(sketch, "E122.7.0.82", {"start": v(739.73, 14.5) * mm, "end": v(724.48, 18.6) * mm});
            skLineSegment(sketch, "E122.7.0.83", {"start": v(718.6, 24.48) * mm, "end": v(714.5, 39.73) * mm});
            skArc(sketch, "E122.7.0.84", {"start": v(724.26, 15.8) * mm, "mid": v(723.4, 15.64) * mm, "end": v(723, 14.84) * mm});
            skArc(sketch, "E122.7.0.85", {"start": v(719.25, -20.25) * mm, "mid": v(719.96, -19.96) * mm, "end": v(720.25, -19.25) * mm});
            skLineSegment(sketch, "E122.7.0.86", {"start": v(743.43, 10.67) * mm, "end": v(724.26, 15.8) * mm});
            skArc(sketch, "E122.7.0.87", {"start": v(685.5, 39.73) * mm, "mid": v(685.15, 41.47) * mm, "end": v(683.56, 42.25) * mm});
            skArc(sketch, "E122.7.0.88", {"start": v(723, 21) * mm, "mid": v(722.41, 22.41) * mm, "end": v(721, 23) * mm});
            skArc(sketch, "E122.7.0.89", {"start": v(739.73, 14.5) * mm, "mid": v(741.47, 14.85) * mm, "end": v(742.25, 16.44) * mm});
            skArc(sketch, "E122.7.0.90", {"start": v(723.09, -8.86) * mm, "mid": v(725, 0) * mm, "end": v(723.09, 8.86) * mm});
            skArc(sketch, "E122.7.0.91", {"start": v(720.3, -7.07) * mm, "mid": v(721.5, 0) * mm, "end": v(720.3, 7.07) * mm});
            skLineSegment(sketch, "E122.7.0.92", {"start": v(714.84, 23) * mm, "end": v(709.27, 23) * mm});
            skArc(sketch, "E122.7.0.93", {"start": v(723, 9.27) * mm, "mid": v(723.02, 9.06) * mm, "end": v(723.09, 8.86) * mm});
            skLineSegment(sketch, "E122.7.0.94", {"start": v(724.26, -15.8) * mm, "end": v(743.43, -10.67) * mm});
            skArc(sketch, "E122.7.0.95", {"start": v(742.25, -16.44) * mm, "mid": v(741.47, -14.85) * mm, "end": v(739.73, -14.5) * mm});
            skArc(sketch, "E122.7.0.96", {"start": v(723.09, -8.86) * mm, "mid": v(723.02, -9.06) * mm, "end": v(723, -9.27) * mm});
            skArc(sketch, "E122.7.0.97", {"start": v(723, -14.84) * mm, "mid": v(723.4, -15.64) * mm, "end": v(724.26, -15.8) * mm});
            skArc(sketch, "E122.7.0.98", {"start": v(716.44, 42.25) * mm, "mid": v(714.85, 41.47) * mm, "end": v(714.5, 39.73) * mm});
            skArc(sketch, "E122.7.0.99", {"start": v(745, -11.88) * mm, "mid": v(744.51, -10.89) * mm, "end": v(743.43, -10.67) * mm});
            skLineSegment(sketch, "E122.7.0.100", {"start": v(723, 20.53) * mm, "end": v(723, 21) * mm});
            skLineSegment(sketch, "E122.7.0.101", {"start": v(723, -9.27) * mm, "end": v(723, -14.84) * mm});
            skLineSegment(sketch, "E122.7.0.102", {"start": v(720.25, 19.25) * mm, "end": v(720.25, 7.4) * mm});
            skLineSegment(sketch, "E122.7.0.103", {"start": v(720.25, -7.4) * mm, "end": v(720.25, -19.25) * mm});
            skLineSegment(sketch, "E122.7.0.104", {"start": v(710.99, 42.25) * mm, "end": v(715.8, 24.26) * mm});
            skLineSegment(sketch, "E122.7.0.105", {"start": v(707.4, 20.25) * mm, "end": v(719.25, 20.25) * mm});
            skArc(sketch, "E122.7.0.106", {"start": v(743.43, 10.67) * mm, "mid": v(744.51, 10.89) * mm, "end": v(745, 11.88) * mm});
            skArc(sketch, "E122.7.0.107", {"start": v(714.84, 23) * mm, "mid": v(715.64, 23.4) * mm, "end": v(715.8, 24.26) * mm});
            skLineSegment(sketch, "E122.7.0.108", {"start": v(724.48, -18.6) * mm, "end": v(739.73, -14.5) * mm});
            skLineSegment(sketch, "E122.7.0.109", {"start": v(723, 14.84) * mm, "end": v(723, 9.27) * mm});
            skArc(sketch, "E122.7.0.110", {"start": v(718.6, 24.48) * mm, "mid": v(719.3, 23.41) * mm, "end": v(720.53, 23) * mm});
            skArc(sketch, "E122.7.0.111", {"start": v(720.25, 19.25) * mm, "mid": v(719.96, 19.96) * mm, "end": v(719.25, 20.25) * mm});
            skArc(sketch, "E122.7.0.112", {"start": v(708.86, 23.09) * mm, "mid": v(709.06, 23.02) * mm, "end": v(709.27, 23) * mm});
            skArc(sketch, "E122.7.0.113", {"start": v(720.3, -7.07) * mm, "mid": v(720.26, -7.23) * mm, "end": v(720.25, -7.4) * mm});
            skArc(sketch, "E122.7.0.114", {"start": v(721, -23) * mm, "mid": v(722.41, -22.41) * mm, "end": v(723, -21) * mm});
            skArc(sketch, "E122.7.0.115", {"start": v(707.07, 20.3) * mm, "mid": v(707.23, 20.26) * mm, "end": v(707.4, 20.25) * mm});
            skArc(sketch, "E122.7.0.116", {"start": v(720.25, 7.4) * mm, "mid": v(720.26, 7.23) * mm, "end": v(720.3, 7.07) * mm});
            skArc(sketch, "E122.7.0.117", {"start": v(723, 20.53) * mm, "mid": v(723.41, 19.3) * mm, "end": v(724.48, 18.6) * mm});
            skLineSegment(sketch, "E122.7.0.118", {"start": v(723, -21) * mm, "end": v(723, -20.53) * mm});
            skLineSegment(sketch, "E122.7.0.119", {"start": v(721, 23) * mm, "end": v(720.53, 23) * mm});
            skLineSegment(sketch, "E122.7.0.120", {"start": v(720.53, -23) * mm, "end": v(721, -23) * mm});
            skArc(sketch, "E122.7.0.121", {"start": v(724.48, -18.6) * mm, "mid": v(723.41, -19.3) * mm, "end": v(723, -20.53) * mm});
            skArc(sketch, "E122.8.0.0", {"start": v(755, -39) * mm, "mid": v(756.76, -43.24) * mm, "end": v(761, -45) * mm});
            skLineSegment(sketch, "E122.8.0.1", {"start": v(755, -39) * mm, "end": v(755, 39) * mm});
            skArc(sketch, "E122.8.0.2", {"start": v(757.75, -39) * mm, "mid": v(758.7, -41.3) * mm, "end": v(761, -42.25) * mm});
            skLineSegment(sketch, "E122.8.0.3", {"start": v(839, -45) * mm, "end": v(761, -45) * mm});
            skLineSegment(sketch, "E122.8.0.4", {"start": v(757.75, -39) * mm, "end": v(757.75, -16.44) * mm});
            skLineSegment(sketch, "E122.8.0.5", {"start": v(783.56, -42.25) * mm, "end": v(761, -42.25) * mm});
            skLineSegment(sketch, "E122.8.0.6", {"start": v(761, 45) * mm, "end": v(839, 45) * mm});
            skArc(sketch, "E122.8.0.7", {"start": v(845, 39) * mm, "mid": v(843.24, 43.24) * mm, "end": v(839, 45) * mm});
            skLineSegment(sketch, "E122.8.0.8", {"start": v(845, 39) * mm, "end": v(845, 11.88) * mm});
            skLineSegment(sketch, "E122.8.0.9", {"start": v(842.25, 39) * mm, "end": v(842.25, 16.44) * mm});
            skLineSegment(sketch, "E122.8.0.10", {"start": v(816.44, 42.25) * mm, "end": v(839, 42.25) * mm});
            skArc(sketch, "E122.8.0.11", {"start": v(842.25, 39) * mm, "mid": v(841.3, 41.3) * mm, "end": v(839, 42.25) * mm});
            skLineSegment(sketch, "E122.8.0.12", {"start": v(757.75, -10.99) * mm, "end": v(757.75, 10.99) * mm});
            skLineSegment(sketch, "E122.8.0.13", {"start": v(789.01, 42.25) * mm, "end": v(810.99, 42.25) * mm});
            skLineSegment(sketch, "E122.8.0.14", {"start": v(842.25, -16.44) * mm, "end": v(842.25, -39) * mm});
            skLineSegment(sketch, "E122.8.0.15", {"start": v(839, -42.25) * mm, "end": v(816.44, -42.25) * mm});
            skLineSegment(sketch, "E122.8.0.16", {"start": v(845, -11.88) * mm, "end": v(845, -39) * mm});
            skArc(sketch, "E122.8.0.17", {"start": v(839, -42.25) * mm, "mid": v(841.3, -41.3) * mm, "end": v(842.25, -39) * mm});
            skArc(sketch, "E122.8.0.18", {"start": v(839, -45) * mm, "mid": v(843.24, -43.24) * mm, "end": v(845, -39) * mm});
            skArc(sketch, "E122.8.0.19", {"start": v(779.47, 23) * mm, "mid": v(780.7, 23.41) * mm, "end": v(781.4, 24.48) * mm});
            skLineSegment(sketch, "E122.8.0.20", {"start": v(760.27, -14.5) * mm, "end": v(775.52, -18.6) * mm});
            skArc(sketch, "E122.8.0.21", {"start": v(761, 42.25) * mm, "mid": v(758.7, 41.3) * mm, "end": v(757.75, 39) * mm});
            skLineSegment(sketch, "E122.8.0.22", {"start": v(757.75, 10.99) * mm, "end": v(775.74, 15.8) * mm});
            skLineSegment(sketch, "E122.8.0.23", {"start": v(757.75, 16.44) * mm, "end": v(757.75, 39) * mm});
            skArc(sketch, "E122.8.0.24", {"start": v(760.27, -14.5) * mm, "mid": v(758.53, -14.85) * mm, "end": v(757.75, -16.44) * mm});
            skLineSegment(sketch, "E122.8.0.25", {"start": v(761, 42.25) * mm, "end": v(783.56, 42.25) * mm});
            skArc(sketch, "E122.8.0.26", {"start": v(780.75, 20.25) * mm, "mid": v(780.04, 19.96) * mm, "end": v(779.75, 19.25) * mm});
            skArc(sketch, "E122.8.0.27", {"start": v(761, 45) * mm, "mid": v(756.76, 43.24) * mm, "end": v(755, 39) * mm});
            skLineSegment(sketch, "E122.8.0.28", {"start": v(775.52, 18.6) * mm, "end": v(760.27, 14.5) * mm});
            skLineSegment(sketch, "E122.8.0.29", {"start": v(775.74, -15.8) * mm, "end": v(757.75, -10.99) * mm});
            skArc(sketch, "E122.8.0.30", {"start": v(757.75, 16.44) * mm, "mid": v(758.53, 14.85) * mm, "end": v(760.27, 14.5) * mm});
            skLineSegment(sketch, "E122.8.0.31", {"start": v(785.5, 39.73) * mm, "end": v(781.4, 24.48) * mm});
            skArc(sketch, "E122.8.0.32", {"start": v(781.4, -24.48) * mm, "mid": v(780.7, -23.41) * mm, "end": v(779.47, -23) * mm});
            skLineSegment(sketch, "E122.8.0.33", {"start": v(777, -9.27) * mm, "end": v(777, -14.84) * mm});
            skArc(sketch, "E122.8.0.34", {"start": v(779.7, 7.07) * mm, "mid": v(779.74, 7.23) * mm, "end": v(779.75, 7.4) * mm});
            skLineSegment(sketch, "E122.8.0.35", {"start": v(777, 21) * mm, "end": v(777, 20.53) * mm});
            skArc(sketch, "E122.8.0.36", {"start": v(809.27, -23) * mm, "mid": v(809.06, -23.02) * mm, "end": v(808.86, -23.09) * mm});
            skArc(sketch, "E122.8.0.37", {"start": v(792.93, -20.3) * mm, "mid": v(800, -21.5) * mm, "end": v(807.07, -20.3) * mm});
            skLineSegment(sketch, "E122.8.0.38", {"start": v(780.75, 20.25) * mm, "end": v(792.6, 20.25) * mm});
            skLineSegment(sketch, "E122.8.0.39", {"start": v(814.5, -39.73) * mm, "end": v(818.6, -24.48) * mm});
            skLineSegment(sketch, "E122.8.0.40", {"start": v(810.99, -42.25) * mm, "end": v(789.01, -42.25) * mm});
            skArc(sketch, "E122.8.0.41", {"start": v(779.75, -7.4) * mm, "mid": v(779.74, -7.23) * mm, "end": v(779.7, -7.07) * mm});
            skLineSegment(sketch, "E122.8.0.42", {"start": v(781.4, -24.48) * mm, "end": v(785.5, -39.73) * mm});
            skLineSegment(sketch, "E122.8.0.43", {"start": v(779.75, -19.25) * mm, "end": v(779.75, -7.4) * mm});
            skArc(sketch, "E122.8.0.44", {"start": v(792.93, -20.3) * mm, "mid": v(792.77, -20.26) * mm, "end": v(792.6, -20.25) * mm});
            skArc(sketch, "E122.8.0.45", {"start": v(776.91, 8.86) * mm, "mid": v(775, 0) * mm, "end": v(776.91, -8.86) * mm});
            skLineSegment(sketch, "E122.8.0.46", {"start": v(785.16, -23) * mm, "end": v(790.73, -23) * mm});
            skArc(sketch, "E122.8.0.47", {"start": v(820.53, -23) * mm, "mid": v(819.3, -23.41) * mm, "end": v(818.6, -24.48) * mm});
            skArc(sketch, "E122.8.0.48", {"start": v(785.16, -23) * mm, "mid": v(784.36, -23.4) * mm, "end": v(784.2, -24.26) * mm});
            skLineSegment(sketch, "E122.8.0.49", {"start": v(815.8, -24.26) * mm, "end": v(810.99, -42.25) * mm});
            skArc(sketch, "E122.8.0.50", {"start": v(775.52, 18.6) * mm, "mid": v(776.59, 19.3) * mm, "end": v(777, 20.53) * mm});
            skArc(sketch, "E122.8.0.51", {"start": v(783.56, -42.25) * mm, "mid": v(785.15, -41.47) * mm, "end": v(785.5, -39.73) * mm});
            skArc(sketch, "E122.8.0.52", {"start": v(777, -9.27) * mm, "mid": v(776.98, -9.06) * mm, "end": v(776.91, -8.86) * mm});
            skArc(sketch, "E122.8.0.53", {"start": v(807.4, -20.25) * mm, "mid": v(807.23, -20.26) * mm, "end": v(807.07, -20.3) * mm});
            skArc(sketch, "E122.8.0.54", {"start": v(779.7, 7.07) * mm, "mid": v(778.5, 0) * mm, "end": v(779.7, -7.07) * mm});
            skLineSegment(sketch, "E122.8.0.55", {"start": v(790.73, 23) * mm, "end": v(785.16, 23) * mm});
            skArc(sketch, "E122.8.0.56", {"start": v(791.14, -23.09) * mm, "mid": v(800, -25) * mm, "end": v(808.86, -23.09) * mm});
            skLineSegment(sketch, "E122.8.0.57", {"start": v(792.6, -20.25) * mm, "end": v(780.75, -20.25) * mm});
            skLineSegment(sketch, "E122.8.0.58", {"start": v(779.75, 7.4) * mm, "end": v(779.75, 19.25) * mm});
            skLineSegment(sketch, "E122.8.0.59", {"start": v(819.25, -20.25) * mm, "end": v(807.4, -20.25) * mm});
            skLineSegment(sketch, "E122.8.0.60", {"start": v(789.01, -42.25) * mm, "end": v(784.2, -24.26) * mm});
            skLineSegment(sketch, "E122.8.0.61", {"start": v(777, -20.53) * mm, "end": v(777, -21) * mm});
            skArc(sketch, "E122.8.0.62", {"start": v(814.5, -39.73) * mm, "mid": v(814.85, -41.47) * mm, "end": v(816.44, -42.25) * mm});
            skArc(sketch, "E122.8.0.63", {"start": v(791.14, -23.09) * mm, "mid": v(790.94, -23.02) * mm, "end": v(790.73, -23) * mm});
            skArc(sketch, "E122.8.0.64", {"start": v(808.86, 23.09) * mm, "mid": v(800, 25) * mm, "end": v(791.14, 23.09) * mm});
            skLineSegment(sketch, "E122.8.0.65", {"start": v(809.27, -23) * mm, "end": v(814.84, -23) * mm});
            skLineSegment(sketch, "E122.8.0.66", {"start": v(777, 14.84) * mm, "end": v(777, 9.27) * mm});
            skLineSegment(sketch, "E122.8.0.67", {"start": v(779.47, 23) * mm, "end": v(779, 23) * mm});
            skArc(sketch, "E122.8.0.68", {"start": v(815.8, -24.26) * mm, "mid": v(815.64, -23.4) * mm, "end": v(814.84, -23) * mm});
            skLineSegment(sketch, "E122.8.0.69", {"start": v(784.2, 24.26) * mm, "end": v(789.01, 42.25) * mm});
            skArc(sketch, "E122.8.0.70", {"start": v(775.74, -15.8) * mm, "mid": v(776.6, -15.64) * mm, "end": v(777, -14.84) * mm});
            skLineSegment(sketch, "E122.8.0.71", {"start": v(779, -23) * mm, "end": v(779.47, -23) * mm});
            skArc(sketch, "E122.8.0.72", {"start": v(777, 14.84) * mm, "mid": v(776.6, 15.64) * mm, "end": v(775.74, 15.8) * mm});
            skArc(sketch, "E122.8.0.73", {"start": v(784.2, 24.26) * mm, "mid": v(784.36, 23.4) * mm, "end": v(785.16, 23) * mm});
            skArc(sketch, "E122.8.0.74", {"start": v(807.07, 20.3) * mm, "mid": v(800, 21.5) * mm, "end": v(792.93, 20.3) * mm});
            skArc(sketch, "E122.8.0.75", {"start": v(777, -21) * mm, "mid": v(777.59, -22.41) * mm, "end": v(779, -23) * mm});
            skArc(sketch, "E122.8.0.76", {"start": v(792.6, 20.25) * mm, "mid": v(792.77, 20.26) * mm, "end": v(792.93, 20.3) * mm});
            skArc(sketch, "E122.8.0.77", {"start": v(779, 23) * mm, "mid": v(777.59, 22.41) * mm, "end": v(777, 21) * mm});
            skArc(sketch, "E122.8.0.78", {"start": v(779.75, -19.25) * mm, "mid": v(780.04, -19.96) * mm, "end": v(780.75, -20.25) * mm});
            skArc(sketch, "E122.8.0.79", {"start": v(790.73, 23) * mm, "mid": v(790.94, 23.02) * mm, "end": v(791.14, 23.09) * mm});
            skArc(sketch, "E122.8.0.80", {"start": v(776.91, 8.86) * mm, "mid": v(776.98, 9.06) * mm, "end": v(777, 9.27) * mm});
            skArc(sketch, "E122.8.0.81", {"start": v(777, -20.53) * mm, "mid": v(776.59, -19.3) * mm, "end": v(775.52, -18.6) * mm});
            skLineSegment(sketch, "E122.8.0.82", {"start": v(839.73, 14.5) * mm, "end": v(824.48, 18.6) * mm});
            skLineSegment(sketch, "E122.8.0.83", {"start": v(818.6, 24.48) * mm, "end": v(814.5, 39.73) * mm});
            skArc(sketch, "E122.8.0.84", {"start": v(824.26, 15.8) * mm, "mid": v(823.4, 15.64) * mm, "end": v(823, 14.84) * mm});
            skArc(sketch, "E122.8.0.85", {"start": v(819.25, -20.25) * mm, "mid": v(819.96, -19.96) * mm, "end": v(820.25, -19.25) * mm});
            skLineSegment(sketch, "E122.8.0.86", {"start": v(843.43, 10.67) * mm, "end": v(824.26, 15.8) * mm});
            skArc(sketch, "E122.8.0.87", {"start": v(785.5, 39.73) * mm, "mid": v(785.15, 41.47) * mm, "end": v(783.56, 42.25) * mm});
            skArc(sketch, "E122.8.0.88", {"start": v(823, 21) * mm, "mid": v(822.41, 22.41) * mm, "end": v(821, 23) * mm});
            skArc(sketch, "E122.8.0.89", {"start": v(839.73, 14.5) * mm, "mid": v(841.47, 14.85) * mm, "end": v(842.25, 16.44) * mm});
            skArc(sketch, "E122.8.0.90", {"start": v(823.09, -8.86) * mm, "mid": v(825, 0) * mm, "end": v(823.09, 8.86) * mm});
            skArc(sketch, "E122.8.0.91", {"start": v(820.3, -7.07) * mm, "mid": v(821.5, 0) * mm, "end": v(820.3, 7.07) * mm});
            skLineSegment(sketch, "E122.8.0.92", {"start": v(814.84, 23) * mm, "end": v(809.27, 23) * mm});
            skArc(sketch, "E122.8.0.93", {"start": v(823, 9.27) * mm, "mid": v(823.02, 9.06) * mm, "end": v(823.09, 8.86) * mm});
            skLineSegment(sketch, "E122.8.0.94", {"start": v(824.26, -15.8) * mm, "end": v(843.43, -10.67) * mm});
            skArc(sketch, "E122.8.0.95", {"start": v(842.25, -16.44) * mm, "mid": v(841.47, -14.85) * mm, "end": v(839.73, -14.5) * mm});
            skArc(sketch, "E122.8.0.96", {"start": v(823.09, -8.86) * mm, "mid": v(823.02, -9.06) * mm, "end": v(823, -9.27) * mm});
            skArc(sketch, "E122.8.0.97", {"start": v(823, -14.84) * mm, "mid": v(823.4, -15.64) * mm, "end": v(824.26, -15.8) * mm});
            skArc(sketch, "E122.8.0.98", {"start": v(816.44, 42.25) * mm, "mid": v(814.85, 41.47) * mm, "end": v(814.5, 39.73) * mm});
            skArc(sketch, "E122.8.0.99", {"start": v(845, -11.88) * mm, "mid": v(844.51, -10.89) * mm, "end": v(843.43, -10.67) * mm});
            skLineSegment(sketch, "E122.8.0.100", {"start": v(823, 20.53) * mm, "end": v(823, 21) * mm});
            skLineSegment(sketch, "E122.8.0.101", {"start": v(823, -9.27) * mm, "end": v(823, -14.84) * mm});
            skLineSegment(sketch, "E122.8.0.102", {"start": v(820.25, 19.25) * mm, "end": v(820.25, 7.4) * mm});
            skLineSegment(sketch, "E122.8.0.103", {"start": v(820.25, -7.4) * mm, "end": v(820.25, -19.25) * mm});
            skLineSegment(sketch, "E122.8.0.104", {"start": v(810.99, 42.25) * mm, "end": v(815.8, 24.26) * mm});
            skLineSegment(sketch, "E122.8.0.105", {"start": v(807.4, 20.25) * mm, "end": v(819.25, 20.25) * mm});
            skArc(sketch, "E122.8.0.106", {"start": v(843.43, 10.67) * mm, "mid": v(844.51, 10.89) * mm, "end": v(845, 11.88) * mm});
            skArc(sketch, "E122.8.0.107", {"start": v(814.84, 23) * mm, "mid": v(815.64, 23.4) * mm, "end": v(815.8, 24.26) * mm});
            skLineSegment(sketch, "E122.8.0.108", {"start": v(824.48, -18.6) * mm, "end": v(839.73, -14.5) * mm});
            skLineSegment(sketch, "E122.8.0.109", {"start": v(823, 14.84) * mm, "end": v(823, 9.27) * mm});
            skArc(sketch, "E122.8.0.110", {"start": v(818.6, 24.48) * mm, "mid": v(819.3, 23.41) * mm, "end": v(820.53, 23) * mm});
            skArc(sketch, "E122.8.0.111", {"start": v(820.25, 19.25) * mm, "mid": v(819.96, 19.96) * mm, "end": v(819.25, 20.25) * mm});
            skArc(sketch, "E122.8.0.112", {"start": v(808.86, 23.09) * mm, "mid": v(809.06, 23.02) * mm, "end": v(809.27, 23) * mm});
            skArc(sketch, "E122.8.0.113", {"start": v(820.3, -7.07) * mm, "mid": v(820.26, -7.23) * mm, "end": v(820.25, -7.4) * mm});
            skArc(sketch, "E122.8.0.114", {"start": v(821, -23) * mm, "mid": v(822.41, -22.41) * mm, "end": v(823, -21) * mm});
            skArc(sketch, "E122.8.0.115", {"start": v(807.07, 20.3) * mm, "mid": v(807.23, 20.26) * mm, "end": v(807.4, 20.25) * mm});
            skArc(sketch, "E122.8.0.116", {"start": v(820.25, 7.4) * mm, "mid": v(820.26, 7.23) * mm, "end": v(820.3, 7.07) * mm});
            skArc(sketch, "E122.8.0.117", {"start": v(823, 20.53) * mm, "mid": v(823.41, 19.3) * mm, "end": v(824.48, 18.6) * mm});
            skLineSegment(sketch, "E122.8.0.118", {"start": v(823, -21) * mm, "end": v(823, -20.53) * mm});
            skLineSegment(sketch, "E122.8.0.119", {"start": v(821, 23) * mm, "end": v(820.53, 23) * mm});
            skLineSegment(sketch, "E122.8.0.120", {"start": v(820.53, -23) * mm, "end": v(821, -23) * mm});
            skArc(sketch, "E122.8.0.121", {"start": v(824.48, -18.6) * mm, "mid": v(823.41, -19.3) * mm, "end": v(823, -20.53) * mm});
            skArc(sketch, "E122.9.0.0", {"start": v(855, -39) * mm, "mid": v(856.76, -43.24) * mm, "end": v(861, -45) * mm});
            skLineSegment(sketch, "E122.9.0.1", {"start": v(855, -39) * mm, "end": v(855, 39) * mm});
            skArc(sketch, "E122.9.0.2", {"start": v(857.75, -39) * mm, "mid": v(858.7, -41.3) * mm, "end": v(861, -42.25) * mm});
            skLineSegment(sketch, "E122.9.0.3", {"start": v(939, -45) * mm, "end": v(861, -45) * mm});
            skLineSegment(sketch, "E122.9.0.4", {"start": v(857.75, -39) * mm, "end": v(857.75, -16.44) * mm});
            skLineSegment(sketch, "E122.9.0.5", {"start": v(883.56, -42.25) * mm, "end": v(861, -42.25) * mm});
            skLineSegment(sketch, "E122.9.0.6", {"start": v(861, 45) * mm, "end": v(939, 45) * mm});
            skArc(sketch, "E122.9.0.7", {"start": v(945, 39) * mm, "mid": v(943.24, 43.24) * mm, "end": v(939, 45) * mm});
            skLineSegment(sketch, "E122.9.0.8", {"start": v(945, 39) * mm, "end": v(945, 11.88) * mm});
            skLineSegment(sketch, "E122.9.0.9", {"start": v(942.25, 39) * mm, "end": v(942.25, 16.44) * mm});
            skLineSegment(sketch, "E122.9.0.10", {"start": v(916.44, 42.25) * mm, "end": v(939, 42.25) * mm});
            skArc(sketch, "E122.9.0.11", {"start": v(942.25, 39) * mm, "mid": v(941.3, 41.3) * mm, "end": v(939, 42.25) * mm});
            skLineSegment(sketch, "E122.9.0.12", {"start": v(857.75, -10.99) * mm, "end": v(857.75, 10.99) * mm});
            skLineSegment(sketch, "E122.9.0.13", {"start": v(889.01, 42.25) * mm, "end": v(910.99, 42.25) * mm});
            skLineSegment(sketch, "E122.9.0.14", {"start": v(942.25, -16.44) * mm, "end": v(942.25, -39) * mm});
            skLineSegment(sketch, "E122.9.0.15", {"start": v(939, -42.25) * mm, "end": v(916.44, -42.25) * mm});
            skLineSegment(sketch, "E122.9.0.16", {"start": v(945, -11.88) * mm, "end": v(945, -39) * mm});
            skArc(sketch, "E122.9.0.17", {"start": v(939, -42.25) * mm, "mid": v(941.3, -41.3) * mm, "end": v(942.25, -39) * mm});
            skArc(sketch, "E122.9.0.18", {"start": v(939, -45) * mm, "mid": v(943.24, -43.24) * mm, "end": v(945, -39) * mm});
            skArc(sketch, "E122.9.0.19", {"start": v(879.47, 23) * mm, "mid": v(880.7, 23.41) * mm, "end": v(881.4, 24.48) * mm});
            skLineSegment(sketch, "E122.9.0.20", {"start": v(860.27, -14.5) * mm, "end": v(875.52, -18.6) * mm});
            skArc(sketch, "E122.9.0.21", {"start": v(861, 42.25) * mm, "mid": v(858.7, 41.3) * mm, "end": v(857.75, 39) * mm});
            skLineSegment(sketch, "E122.9.0.22", {"start": v(857.75, 10.99) * mm, "end": v(875.74, 15.8) * mm});
            skLineSegment(sketch, "E122.9.0.23", {"start": v(857.75, 16.44) * mm, "end": v(857.75, 39) * mm});
            skArc(sketch, "E122.9.0.24", {"start": v(860.27, -14.5) * mm, "mid": v(858.53, -14.85) * mm, "end": v(857.75, -16.44) * mm});
            skLineSegment(sketch, "E122.9.0.25", {"start": v(861, 42.25) * mm, "end": v(883.56, 42.25) * mm});
            skArc(sketch, "E122.9.0.26", {"start": v(880.75, 20.25) * mm, "mid": v(880.04, 19.96) * mm, "end": v(879.75, 19.25) * mm});
            skArc(sketch, "E122.9.0.27", {"start": v(861, 45) * mm, "mid": v(856.76, 43.24) * mm, "end": v(855, 39) * mm});
            skLineSegment(sketch, "E122.9.0.28", {"start": v(875.52, 18.6) * mm, "end": v(860.27, 14.5) * mm});
            skLineSegment(sketch, "E122.9.0.29", {"start": v(875.74, -15.8) * mm, "end": v(857.75, -10.99) * mm});
            skArc(sketch, "E122.9.0.30", {"start": v(857.75, 16.44) * mm, "mid": v(858.53, 14.85) * mm, "end": v(860.27, 14.5) * mm});
            skLineSegment(sketch, "E122.9.0.31", {"start": v(885.5, 39.73) * mm, "end": v(881.4, 24.48) * mm});
            skArc(sketch, "E122.9.0.32", {"start": v(881.4, -24.48) * mm, "mid": v(880.7, -23.41) * mm, "end": v(879.47, -23) * mm});
            skLineSegment(sketch, "E122.9.0.33", {"start": v(877, -9.27) * mm, "end": v(877, -14.84) * mm});
            skArc(sketch, "E122.9.0.34", {"start": v(879.7, 7.07) * mm, "mid": v(879.74, 7.23) * mm, "end": v(879.75, 7.4) * mm});
            skLineSegment(sketch, "E122.9.0.35", {"start": v(877, 21) * mm, "end": v(877, 20.53) * mm});
            skArc(sketch, "E122.9.0.36", {"start": v(909.27, -23) * mm, "mid": v(909.06, -23.02) * mm, "end": v(908.86, -23.09) * mm});
            skArc(sketch, "E122.9.0.37", {"start": v(892.93, -20.3) * mm, "mid": v(900, -21.5) * mm, "end": v(907.07, -20.3) * mm});
            skLineSegment(sketch, "E122.9.0.38", {"start": v(880.75, 20.25) * mm, "end": v(892.6, 20.25) * mm});
            skLineSegment(sketch, "E122.9.0.39", {"start": v(914.5, -39.73) * mm, "end": v(918.6, -24.48) * mm});
            skLineSegment(sketch, "E122.9.0.40", {"start": v(910.99, -42.25) * mm, "end": v(889.01, -42.25) * mm});
            skArc(sketch, "E122.9.0.41", {"start": v(879.75, -7.4) * mm, "mid": v(879.74, -7.23) * mm, "end": v(879.7, -7.07) * mm});
            skLineSegment(sketch, "E122.9.0.42", {"start": v(881.4, -24.48) * mm, "end": v(885.5, -39.73) * mm});
            skLineSegment(sketch, "E122.9.0.43", {"start": v(879.75, -19.25) * mm, "end": v(879.75, -7.4) * mm});
            skArc(sketch, "E122.9.0.44", {"start": v(892.93, -20.3) * mm, "mid": v(892.77, -20.26) * mm, "end": v(892.6, -20.25) * mm});
            skArc(sketch, "E122.9.0.45", {"start": v(876.91, 8.86) * mm, "mid": v(875, 0) * mm, "end": v(876.91, -8.86) * mm});
            skLineSegment(sketch, "E122.9.0.46", {"start": v(885.16, -23) * mm, "end": v(890.73, -23) * mm});
            skArc(sketch, "E122.9.0.47", {"start": v(920.53, -23) * mm, "mid": v(919.3, -23.41) * mm, "end": v(918.6, -24.48) * mm});
            skArc(sketch, "E122.9.0.48", {"start": v(885.16, -23) * mm, "mid": v(884.36, -23.4) * mm, "end": v(884.2, -24.26) * mm});
            skLineSegment(sketch, "E122.9.0.49", {"start": v(915.8, -24.26) * mm, "end": v(910.99, -42.25) * mm});
            skArc(sketch, "E122.9.0.50", {"start": v(875.52, 18.6) * mm, "mid": v(876.59, 19.3) * mm, "end": v(877, 20.53) * mm});
            skArc(sketch, "E122.9.0.51", {"start": v(883.56, -42.25) * mm, "mid": v(885.15, -41.47) * mm, "end": v(885.5, -39.73) * mm});
            skArc(sketch, "E122.9.0.52", {"start": v(877, -9.27) * mm, "mid": v(876.98, -9.06) * mm, "end": v(876.91, -8.86) * mm});
            skArc(sketch, "E122.9.0.53", {"start": v(907.4, -20.25) * mm, "mid": v(907.23, -20.26) * mm, "end": v(907.07, -20.3) * mm});
            skArc(sketch, "E122.9.0.54", {"start": v(879.7, 7.07) * mm, "mid": v(878.5, 0) * mm, "end": v(879.7, -7.07) * mm});
            skLineSegment(sketch, "E122.9.0.55", {"start": v(890.73, 23) * mm, "end": v(885.16, 23) * mm});
            skArc(sketch, "E122.9.0.56", {"start": v(891.14, -23.09) * mm, "mid": v(900, -25) * mm, "end": v(908.86, -23.09) * mm});
            skLineSegment(sketch, "E122.9.0.57", {"start": v(892.6, -20.25) * mm, "end": v(880.75, -20.25) * mm});
            skLineSegment(sketch, "E122.9.0.58", {"start": v(879.75, 7.4) * mm, "end": v(879.75, 19.25) * mm});
            skLineSegment(sketch, "E122.9.0.59", {"start": v(919.25, -20.25) * mm, "end": v(907.4, -20.25) * mm});
            skLineSegment(sketch, "E122.9.0.60", {"start": v(889.01, -42.25) * mm, "end": v(884.2, -24.26) * mm});
            skLineSegment(sketch, "E122.9.0.61", {"start": v(877, -20.53) * mm, "end": v(877, -21) * mm});
            skArc(sketch, "E122.9.0.62", {"start": v(914.5, -39.73) * mm, "mid": v(914.85, -41.47) * mm, "end": v(916.44, -42.25) * mm});
            skArc(sketch, "E122.9.0.63", {"start": v(891.14, -23.09) * mm, "mid": v(890.94, -23.02) * mm, "end": v(890.73, -23) * mm});
            skArc(sketch, "E122.9.0.64", {"start": v(908.86, 23.09) * mm, "mid": v(900, 25) * mm, "end": v(891.14, 23.09) * mm});
            skLineSegment(sketch, "E122.9.0.65", {"start": v(909.27, -23) * mm, "end": v(914.84, -23) * mm});
            skLineSegment(sketch, "E122.9.0.66", {"start": v(877, 14.84) * mm, "end": v(877, 9.27) * mm});
            skLineSegment(sketch, "E122.9.0.67", {"start": v(879.47, 23) * mm, "end": v(879, 23) * mm});
            skArc(sketch, "E122.9.0.68", {"start": v(915.8, -24.26) * mm, "mid": v(915.64, -23.4) * mm, "end": v(914.84, -23) * mm});
            skLineSegment(sketch, "E122.9.0.69", {"start": v(884.2, 24.26) * mm, "end": v(889.01, 42.25) * mm});
            skArc(sketch, "E122.9.0.70", {"start": v(875.74, -15.8) * mm, "mid": v(876.6, -15.64) * mm, "end": v(877, -14.84) * mm});
            skLineSegment(sketch, "E122.9.0.71", {"start": v(879, -23) * mm, "end": v(879.47, -23) * mm});
            skArc(sketch, "E122.9.0.72", {"start": v(877, 14.84) * mm, "mid": v(876.6, 15.64) * mm, "end": v(875.74, 15.8) * mm});
            skArc(sketch, "E122.9.0.73", {"start": v(884.2, 24.26) * mm, "mid": v(884.36, 23.4) * mm, "end": v(885.16, 23) * mm});
            skArc(sketch, "E122.9.0.74", {"start": v(907.07, 20.3) * mm, "mid": v(900, 21.5) * mm, "end": v(892.93, 20.3) * mm});
            skArc(sketch, "E122.9.0.75", {"start": v(877, -21) * mm, "mid": v(877.59, -22.41) * mm, "end": v(879, -23) * mm});
            skArc(sketch, "E122.9.0.76", {"start": v(892.6, 20.25) * mm, "mid": v(892.77, 20.26) * mm, "end": v(892.93, 20.3) * mm});
            skArc(sketch, "E122.9.0.77", {"start": v(879, 23) * mm, "mid": v(877.59, 22.41) * mm, "end": v(877, 21) * mm});
            skArc(sketch, "E122.9.0.78", {"start": v(879.75, -19.25) * mm, "mid": v(880.04, -19.96) * mm, "end": v(880.75, -20.25) * mm});
            skArc(sketch, "E122.9.0.79", {"start": v(890.73, 23) * mm, "mid": v(890.94, 23.02) * mm, "end": v(891.14, 23.09) * mm});
            skArc(sketch, "E122.9.0.80", {"start": v(876.91, 8.86) * mm, "mid": v(876.98, 9.06) * mm, "end": v(877, 9.27) * mm});
            skArc(sketch, "E122.9.0.81", {"start": v(877, -20.53) * mm, "mid": v(876.59, -19.3) * mm, "end": v(875.52, -18.6) * mm});
            skLineSegment(sketch, "E122.9.0.82", {"start": v(939.73, 14.5) * mm, "end": v(924.48, 18.6) * mm});
            skLineSegment(sketch, "E122.9.0.83", {"start": v(918.6, 24.48) * mm, "end": v(914.5, 39.73) * mm});
            skArc(sketch, "E122.9.0.84", {"start": v(924.26, 15.8) * mm, "mid": v(923.4, 15.64) * mm, "end": v(923, 14.84) * mm});
            skArc(sketch, "E122.9.0.85", {"start": v(919.25, -20.25) * mm, "mid": v(919.96, -19.96) * mm, "end": v(920.25, -19.25) * mm});
            skLineSegment(sketch, "E122.9.0.86", {"start": v(943.43, 10.67) * mm, "end": v(924.26, 15.8) * mm});
            skArc(sketch, "E122.9.0.87", {"start": v(885.5, 39.73) * mm, "mid": v(885.15, 41.47) * mm, "end": v(883.56, 42.25) * mm});
            skArc(sketch, "E122.9.0.88", {"start": v(923, 21) * mm, "mid": v(922.41, 22.41) * mm, "end": v(921, 23) * mm});
            skArc(sketch, "E122.9.0.89", {"start": v(939.73, 14.5) * mm, "mid": v(941.47, 14.85) * mm, "end": v(942.25, 16.44) * mm});
            skArc(sketch, "E122.9.0.90", {"start": v(923.09, -8.86) * mm, "mid": v(925, 0) * mm, "end": v(923.09, 8.86) * mm});
            skArc(sketch, "E122.9.0.91", {"start": v(920.3, -7.07) * mm, "mid": v(921.5, 0) * mm, "end": v(920.3, 7.07) * mm});
            skLineSegment(sketch, "E122.9.0.92", {"start": v(914.84, 23) * mm, "end": v(909.27, 23) * mm});
            skArc(sketch, "E122.9.0.93", {"start": v(923, 9.27) * mm, "mid": v(923.02, 9.06) * mm, "end": v(923.09, 8.86) * mm});
            skLineSegment(sketch, "E122.9.0.94", {"start": v(924.26, -15.8) * mm, "end": v(943.43, -10.67) * mm});
            skArc(sketch, "E122.9.0.95", {"start": v(942.25, -16.44) * mm, "mid": v(941.47, -14.85) * mm, "end": v(939.73, -14.5) * mm});
            skArc(sketch, "E122.9.0.96", {"start": v(923.09, -8.86) * mm, "mid": v(923.02, -9.06) * mm, "end": v(923, -9.27) * mm});
            skArc(sketch, "E122.9.0.97", {"start": v(923, -14.84) * mm, "mid": v(923.4, -15.64) * mm, "end": v(924.26, -15.8) * mm});
            skArc(sketch, "E122.9.0.98", {"start": v(916.44, 42.25) * mm, "mid": v(914.85, 41.47) * mm, "end": v(914.5, 39.73) * mm});
            skArc(sketch, "E122.9.0.99", {"start": v(945, -11.88) * mm, "mid": v(944.51, -10.89) * mm, "end": v(943.43, -10.67) * mm});
            skLineSegment(sketch, "E122.9.0.100", {"start": v(923, 20.53) * mm, "end": v(923, 21) * mm});
            skLineSegment(sketch, "E122.9.0.101", {"start": v(923, -9.27) * mm, "end": v(923, -14.84) * mm});
            skLineSegment(sketch, "E122.9.0.102", {"start": v(920.25, 19.25) * mm, "end": v(920.25, 7.4) * mm});
            skLineSegment(sketch, "E122.9.0.103", {"start": v(920.25, -7.4) * mm, "end": v(920.25, -19.25) * mm});
            skLineSegment(sketch, "E122.9.0.104", {"start": v(910.99, 42.25) * mm, "end": v(915.8, 24.26) * mm});
            skLineSegment(sketch, "E122.9.0.105", {"start": v(907.4, 20.25) * mm, "end": v(919.25, 20.25) * mm});
            skArc(sketch, "E122.9.0.106", {"start": v(943.43, 10.67) * mm, "mid": v(944.51, 10.89) * mm, "end": v(945, 11.88) * mm});
            skArc(sketch, "E122.9.0.107", {"start": v(914.84, 23) * mm, "mid": v(915.64, 23.4) * mm, "end": v(915.8, 24.26) * mm});
            skLineSegment(sketch, "E122.9.0.108", {"start": v(924.48, -18.6) * mm, "end": v(939.73, -14.5) * mm});
            skLineSegment(sketch, "E122.9.0.109", {"start": v(923, 14.84) * mm, "end": v(923, 9.27) * mm});
            skArc(sketch, "E122.9.0.110", {"start": v(918.6, 24.48) * mm, "mid": v(919.3, 23.41) * mm, "end": v(920.53, 23) * mm});
            skArc(sketch, "E122.9.0.111", {"start": v(920.25, 19.25) * mm, "mid": v(919.96, 19.96) * mm, "end": v(919.25, 20.25) * mm});
            skArc(sketch, "E122.9.0.112", {"start": v(908.86, 23.09) * mm, "mid": v(909.06, 23.02) * mm, "end": v(909.27, 23) * mm});
            skArc(sketch, "E122.9.0.113", {"start": v(920.3, -7.07) * mm, "mid": v(920.26, -7.23) * mm, "end": v(920.25, -7.4) * mm});
            skArc(sketch, "E122.9.0.114", {"start": v(921, -23) * mm, "mid": v(922.41, -22.41) * mm, "end": v(923, -21) * mm});
            skArc(sketch, "E122.9.0.115", {"start": v(907.07, 20.3) * mm, "mid": v(907.23, 20.26) * mm, "end": v(907.4, 20.25) * mm});
            skArc(sketch, "E122.9.0.116", {"start": v(920.25, 7.4) * mm, "mid": v(920.26, 7.23) * mm, "end": v(920.3, 7.07) * mm});
            skArc(sketch, "E122.9.0.117", {"start": v(923, 20.53) * mm, "mid": v(923.41, 19.3) * mm, "end": v(924.48, 18.6) * mm});
            skLineSegment(sketch, "E122.9.0.118", {"start": v(923, -21) * mm, "end": v(923, -20.53) * mm});
            skLineSegment(sketch, "E122.9.0.119", {"start": v(921, 23) * mm, "end": v(920.53, 23) * mm});
            skLineSegment(sketch, "E122.9.0.120", {"start": v(920.53, -23) * mm, "end": v(921, -23) * mm});
            skArc(sketch, "E122.9.0.121", {"start": v(924.48, -18.6) * mm, "mid": v(923.41, -19.3) * mm, "end": v(923, -20.53) * mm});
            skLineSegment(sketch, "E122.direction1", {"start": v(-39, -45) * mm, "end": v(61, -45) * mm, "construction": true});
            skSolve(sketch);
        }
        {
            var Q0;
            Q0=makeQuery(id+"F0.imprint","IMPRINT",FACE,{"disambiguationData":[TD([[makeQuery(id+"F0.imprint","IMPRINT",EDGE,{"derivedFrom":sQuery(id+"F0.wireOp",EDGE,"E0")}),1.0]])]});
            extrude(context, id + "F1", {"entities" : qUnion([Q0]), "depth" : 1000 * mm, "offsetDistance" : 25 * mm});
        }
    });
